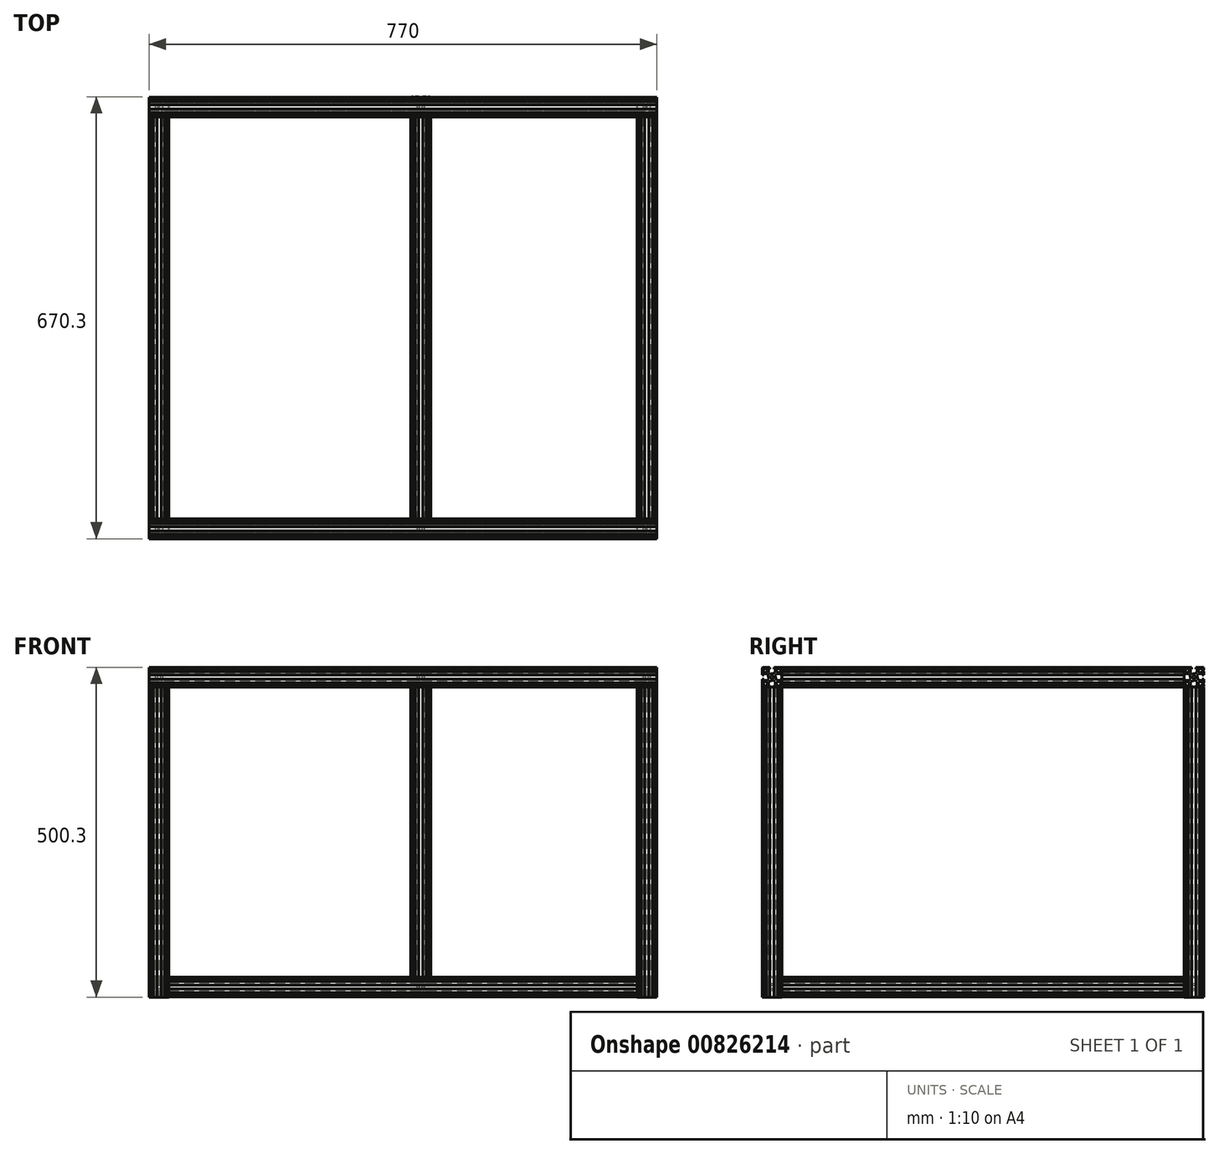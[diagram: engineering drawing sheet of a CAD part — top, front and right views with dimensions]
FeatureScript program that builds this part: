
annotation { "Feature Type Name" : "Feature", "Feature Type Description" : "" }
export const myFeature = defineFeature(function(context is Context, id is Id, definition is map)
    precondition{}
    {
        {
            var Q0;
            Q0=qCreatedBy(makeId("Top.planeOp"),FACE);
            var sketch = newSketch(context, id + "F0", { "sketchPlane" : qUnion([Q0])});
            skLineSegment(sketch, "E0", {"start": v(-2.6, 15) * mm, "end": v(32.7, 15) * mm});
            skLineSegment(sketch, "E1", {"start": v(15, 32.3) * mm, "end": v(15, -1.8) * mm});
            skLineSegment(sketch, "E2", {"start": v(19.2, 25) * mm, "end": v(32.7, 25) * mm});
            skLineSegment(sketch, "E3", {"start": v(25, 32.3) * mm, "end": v(25, 18.9) * mm});
            skLineSegment(sketch, "E4", {"start": v(10.8, 25) * mm, "end": v(-2.7, 25) * mm});
            skLineSegment(sketch, "E5", {"start": v(5, 32.3) * mm, "end": v(5, 18.9) * mm});
            skLineSegment(sketch, "E6", {"start": v(19.2, 5) * mm, "end": v(32.7, 5) * mm});
            skLineSegment(sketch, "E7", {"start": v(10.8, 5) * mm, "end": v(-2.7, 5) * mm});
            skLineSegment(sketch, "E8", {"start": v(5, -2.3) * mm, "end": v(5, 11.1) * mm});
            skLineSegment(sketch, "E9", {"start": v(18.15, 30) * mm, "end": v(18.15, 27.5) * mm});
            skLineSegment(sketch, "E10", {"start": v(20.15, 27.5) * mm, "end": v(20.15, 21.55) * mm});
            skLineSegment(sketch, "E11", {"start": v(18.15, 27.5) * mm, "end": v(20.15, 27.5) * mm});
            skLineSegment(sketch, "E12", {"start": v(11.85, 30) * mm, "end": v(11.85, 27.5) * mm});
            skLineSegment(sketch, "E13", {"start": v(11.85, 27.5) * mm, "end": v(9.85, 27.5) * mm});
            skLineSegment(sketch, "E14", {"start": v(9.85, 27.5) * mm, "end": v(9.85, 21.55) * mm});
            skLineSegment(sketch, "E15", {"start": v(0, 18.15) * mm, "end": v(2.5, 18.15) * mm});
            skLineSegment(sketch, "E16", {"start": v(2.5, 20.15) * mm, "end": v(8.45, 20.15) * mm});
            skLineSegment(sketch, "E17", {"start": v(2.5, 18.15) * mm, "end": v(2.5, 20.15) * mm});
            skLineSegment(sketch, "E18", {"start": v(0, 11.85) * mm, "end": v(2.5, 11.85) * mm});
            skLineSegment(sketch, "E19", {"start": v(2.5, 11.85) * mm, "end": v(2.5, 9.85) * mm});
            skLineSegment(sketch, "E20", {"start": v(2.5, 9.85) * mm, "end": v(8.45, 9.85) * mm});
            skLineSegment(sketch, "E21", {"start": v(11.85, 0) * mm, "end": v(11.85, 2.5) * mm});
            skLineSegment(sketch, "E22", {"start": v(9.85, 2.5) * mm, "end": v(9.85, 8.45) * mm});
            skLineSegment(sketch, "E23", {"start": v(11.85, 2.5) * mm, "end": v(9.85, 2.5) * mm});
            skLineSegment(sketch, "E24", {"start": v(18.15, 0) * mm, "end": v(18.15, 2.5) * mm});
            skLineSegment(sketch, "E25", {"start": v(18.15, 2.5) * mm, "end": v(20.15, 2.5) * mm});
            skLineSegment(sketch, "E26", {"start": v(20.15, 2.5) * mm, "end": v(20.15, 8.45) * mm});
            skLineSegment(sketch, "E27", {"start": v(30, 11.85) * mm, "end": v(27.5, 11.85) * mm});
            skLineSegment(sketch, "E28", {"start": v(27.5, 9.85) * mm, "end": v(21.55, 9.85) * mm});
            skLineSegment(sketch, "E29", {"start": v(27.5, 11.85) * mm, "end": v(27.5, 9.85) * mm});
            skLineSegment(sketch, "E30", {"start": v(30, 18.15) * mm, "end": v(27.5, 18.15) * mm});
            skLineSegment(sketch, "E31", {"start": v(27.5, 18.15) * mm, "end": v(27.5, 20.15) * mm});
            skLineSegment(sketch, "E32", {"start": v(27.5, 20.15) * mm, "end": v(21.55, 20.15) * mm});
            skLineSegment(sketch, "E33", {"start": v(11.85, 19.5) * mm, "end": v(11.85, 21.55) * mm});
            skLineSegment(sketch, "E34", {"start": v(9.85, 21.55) * mm, "end": v(11.85, 21.55) * mm});
            skLineSegment(sketch, "E35", {"start": v(11.85, 19.5) * mm, "end": v(20.15, 21.55) * mm});
            skLineSegment(sketch, "E36", {"start": v(10.5, 11.85) * mm, "end": v(8.45, 11.85) * mm});
            skLineSegment(sketch, "E37", {"start": v(8.45, 9.85) * mm, "end": v(8.45, 11.85) * mm});
            skLineSegment(sketch, "E38", {"start": v(10.5, 11.85) * mm, "end": v(8.45, 20.15) * mm});
            skLineSegment(sketch, "E39", {"start": v(18.15, 10.5) * mm, "end": v(18.15, 8.45) * mm});
            skLineSegment(sketch, "E40", {"start": v(20.15, 8.45) * mm, "end": v(18.15, 8.45) * mm});
            skLineSegment(sketch, "E41", {"start": v(18.15, 10.5) * mm, "end": v(9.85, 8.45) * mm});
            skLineSegment(sketch, "E42", {"start": v(19.5, 18.15) * mm, "end": v(21.55, 18.15) * mm});
            skLineSegment(sketch, "E43", {"start": v(21.55, 20.15) * mm, "end": v(21.55, 18.15) * mm});
            skLineSegment(sketch, "E44", {"start": v(19.5, 18.15) * mm, "end": v(21.55, 9.85) * mm});
            skCircle(sketch, "E45", {"center": v(15, 15) * mm, "radius": 2.5 * mm});
            skLineSegment(sketch, "E46", {"start": v(28, 26.24) * mm, "end": v(26.24, 28) * mm});
            skLineSegment(sketch, "E47", {"start": v(26.24, 28) * mm, "end": v(23.76, 28) * mm});
            skLineSegment(sketch, "E48", {"start": v(23.76, 28) * mm, "end": v(22, 26.24) * mm});
            skLineSegment(sketch, "E49", {"start": v(22, 26.24) * mm, "end": v(22, 23.76) * mm});
            skLineSegment(sketch, "E50", {"start": v(22, 23.76) * mm, "end": v(23.76, 22) * mm});
            skLineSegment(sketch, "E51", {"start": v(23.76, 22) * mm, "end": v(26.24, 22) * mm});
            skLineSegment(sketch, "E52", {"start": v(26.24, 22) * mm, "end": v(28, 23.76) * mm});
            skLineSegment(sketch, "E53", {"start": v(28, 23.76) * mm, "end": v(28, 26.24) * mm});
            skLineSegment(sketch, "E54", {"start": v(8, 26.24) * mm, "end": v(6.24, 28) * mm});
            skLineSegment(sketch, "E55", {"start": v(6.24, 28) * mm, "end": v(3.76, 28) * mm});
            skLineSegment(sketch, "E56", {"start": v(3.76, 28) * mm, "end": v(2, 26.24) * mm});
            skLineSegment(sketch, "E57", {"start": v(2, 26.24) * mm, "end": v(2, 23.76) * mm});
            skLineSegment(sketch, "E58", {"start": v(2, 23.76) * mm, "end": v(3.76, 22) * mm});
            skLineSegment(sketch, "E59", {"start": v(3.76, 22) * mm, "end": v(6.24, 22) * mm});
            skLineSegment(sketch, "E60", {"start": v(6.24, 22) * mm, "end": v(8, 23.76) * mm});
            skLineSegment(sketch, "E61", {"start": v(8, 23.76) * mm, "end": v(8, 26.24) * mm});
            skLineSegment(sketch, "E62", {"start": v(28, 6.24) * mm, "end": v(26.24, 8) * mm});
            skLineSegment(sketch, "E63", {"start": v(26.24, 8) * mm, "end": v(23.76, 8) * mm});
            skLineSegment(sketch, "E64", {"start": v(23.76, 8) * mm, "end": v(22, 6.24) * mm});
            skLineSegment(sketch, "E65", {"start": v(22, 6.24) * mm, "end": v(22, 3.76) * mm});
            skLineSegment(sketch, "E66", {"start": v(22, 3.76) * mm, "end": v(23.76, 2) * mm});
            skLineSegment(sketch, "E67", {"start": v(23.76, 2) * mm, "end": v(26.24, 2) * mm});
            skLineSegment(sketch, "E68", {"start": v(26.24, 2) * mm, "end": v(28, 3.76) * mm});
            skLineSegment(sketch, "E69", {"start": v(28, 3.76) * mm, "end": v(28, 6.24) * mm});
            skLineSegment(sketch, "E70", {"start": v(8, 6.24) * mm, "end": v(6.24, 8) * mm});
            skLineSegment(sketch, "E71", {"start": v(6.24, 8) * mm, "end": v(3.76, 8) * mm});
            skLineSegment(sketch, "E72", {"start": v(3.76, 8) * mm, "end": v(2, 6.24) * mm});
            skLineSegment(sketch, "E73", {"start": v(2, 6.24) * mm, "end": v(2, 3.76) * mm});
            skLineSegment(sketch, "E74", {"start": v(2, 3.76) * mm, "end": v(3.76, 2) * mm});
            skLineSegment(sketch, "E75", {"start": v(3.76, 2) * mm, "end": v(6.24, 2) * mm});
            skLineSegment(sketch, "E76", {"start": v(6.24, 2) * mm, "end": v(8, 3.76) * mm});
            skLineSegment(sketch, "E77", {"start": v(8, 3.76) * mm, "end": v(8, 6.24) * mm});
            skLineSegment(sketch, "E78", {"start": v(26.5, 30) * mm, "end": v(26.5, 29.7) * mm});
            skLineSegment(sketch, "E79", {"start": v(26.5, 29.7) * mm, "end": v(25, 29.7) * mm});
            skLineSegment(sketch, "E80", {"start": v(23.5, 30) * mm, "end": v(23.5, 29.7) * mm});
            skLineSegment(sketch, "E81", {"start": v(23.5, 29.7) * mm, "end": v(25, 29.7) * mm});
            skLineSegment(sketch, "E82", {"start": v(30, 23.5) * mm, "end": v(29.7, 23.5) * mm});
            skLineSegment(sketch, "E83", {"start": v(29.7, 23.5) * mm, "end": v(29.7, 25) * mm});
            skLineSegment(sketch, "E84", {"start": v(30, 26.5) * mm, "end": v(29.7, 26.5) * mm});
            skLineSegment(sketch, "E85", {"start": v(29.7, 26.5) * mm, "end": v(29.7, 25) * mm});
            skLineSegment(sketch, "E86", {"start": v(25, -2.3) * mm, "end": v(25, 11.1) * mm});
            skLineSegment(sketch, "E87", {"start": v(26.5, 0) * mm, "end": v(26.5, 0.3) * mm});
            skLineSegment(sketch, "E88", {"start": v(26.5, 0.3) * mm, "end": v(25, 0.3) * mm});
            skLineSegment(sketch, "E89", {"start": v(23.5, 0) * mm, "end": v(23.5, 0.3) * mm});
            skLineSegment(sketch, "E90", {"start": v(23.5, 0.3) * mm, "end": v(25, 0.3) * mm});
            skLineSegment(sketch, "E91", {"start": v(30, 6.5) * mm, "end": v(29.7, 6.5) * mm});
            skLineSegment(sketch, "E92", {"start": v(29.7, 6.5) * mm, "end": v(29.7, 5) * mm});
            skLineSegment(sketch, "E93", {"start": v(30, 3.5) * mm, "end": v(29.7, 3.5) * mm});
            skLineSegment(sketch, "E94", {"start": v(29.7, 3.5) * mm, "end": v(29.7, 5) * mm});
            skLineSegment(sketch, "E95", {"start": v(3.5, 30) * mm, "end": v(3.5, 29.7) * mm});
            skLineSegment(sketch, "E96", {"start": v(3.5, 29.7) * mm, "end": v(5, 29.7) * mm});
            skLineSegment(sketch, "E97", {"start": v(6.5, 30) * mm, "end": v(6.5, 29.7) * mm});
            skLineSegment(sketch, "E98", {"start": v(6.5, 29.7) * mm, "end": v(5, 29.7) * mm});
            skLineSegment(sketch, "E99", {"start": v(0, 23.5) * mm, "end": v(0.3, 23.5) * mm});
            skLineSegment(sketch, "E100", {"start": v(0.3, 23.5) * mm, "end": v(0.3, 25) * mm});
            skLineSegment(sketch, "E101", {"start": v(0, 26.5) * mm, "end": v(0.3, 26.5) * mm});
            skLineSegment(sketch, "E102", {"start": v(0.3, 26.5) * mm, "end": v(0.3, 25) * mm});
            skLineSegment(sketch, "E103", {"start": v(0, 6.5) * mm, "end": v(0.3, 6.5) * mm});
            skLineSegment(sketch, "E104", {"start": v(0.3, 6.5) * mm, "end": v(0.3, 5) * mm});
            skLineSegment(sketch, "E105", {"start": v(0, 3.5) * mm, "end": v(0.3, 3.5) * mm});
            skLineSegment(sketch, "E106", {"start": v(0.3, 3.5) * mm, "end": v(0.3, 5) * mm});
            skLineSegment(sketch, "E107", {"start": v(3.5, 0) * mm, "end": v(3.5, 0.3) * mm});
            skLineSegment(sketch, "E108", {"start": v(3.5, 0.3) * mm, "end": v(5, 0.3) * mm});
            skLineSegment(sketch, "E109", {"start": v(6.5, 0) * mm, "end": v(6.5, 0.3) * mm});
            skLineSegment(sketch, "E110", {"start": v(6.5, 0.3) * mm, "end": v(5, 0.3) * mm});
            skLineSegment(sketch, "E111", {"start": v(29, 30) * mm, "end": v(26.5, 30) * mm});
            skLineSegment(sketch, "E112", {"start": v(23.5, 30) * mm, "end": v(18.15, 30) * mm});
            skLineSegment(sketch, "E113", {"start": v(30, 18.15) * mm, "end": v(30, 23.5) * mm});
            skLineSegment(sketch, "E114", {"start": v(30, 29) * mm, "end": v(30, 26.5) * mm});
            skLineSegment(sketch, "E115", {"start": v(30, 1) * mm, "end": v(30, 3.5) * mm});
            skLineSegment(sketch, "E116", {"start": v(30, 6.5) * mm, "end": v(30, 11.85) * mm});
            skLineSegment(sketch, "E117", {"start": v(18.15, 0) * mm, "end": v(23.5, 0) * mm});
            skLineSegment(sketch, "E118", {"start": v(29, 0) * mm, "end": v(26.5, 0) * mm});
            skLineSegment(sketch, "E119", {"start": v(1, 0) * mm, "end": v(3.5, 0) * mm});
            skLineSegment(sketch, "E120", {"start": v(6.5, 0) * mm, "end": v(11.85, 0) * mm});
            skLineSegment(sketch, "E121", {"start": v(0, 11.85) * mm, "end": v(0, 6.5) * mm});
            skLineSegment(sketch, "E122", {"start": v(0, 1) * mm, "end": v(0, 3.5) * mm});
            skLineSegment(sketch, "E123", {"start": v(0, 29) * mm, "end": v(0, 26.5) * mm});
            skLineSegment(sketch, "E124", {"start": v(0, 23.5) * mm, "end": v(0, 18.15) * mm});
            skLineSegment(sketch, "E125", {"start": v(11.85, 30) * mm, "end": v(6.5, 30) * mm});
            skLineSegment(sketch, "E126", {"start": v(1, 30) * mm, "end": v(3.5, 30) * mm});
            skLineSegment(sketch, "E127", {"start": v(1, 30) * mm, "end": v(0, 29) * mm});
            skLineSegment(sketch, "E128", {"start": v(0, 1) * mm, "end": v(1, 0) * mm});
            skLineSegment(sketch, "E129", {"start": v(29, 0) * mm, "end": v(30, 1) * mm});
            skLineSegment(sketch, "E130", {"start": v(30, 29) * mm, "end": v(29, 30) * mm});
            skSolve(sketch);
        }
        {
            var Q0;
            {var subQ0=sQuery(id+"F0.wireOp",EDGE,"E76");Q0=makeQuery(id+"F0.imprint","IMPRINT",FACE,{"disambiguationData":[TD([[makeQuery(id+"F0.imprint","IMPRINT",EDGE,{"derivedFrom":subQ0}),1.0]])]});}
            var Q1;
            {var subQ0=sQuery(id+"F0.wireOp",EDGE,"E72");Q1=makeQuery(id+"F0.imprint","IMPRINT",FACE,{"disambiguationData":[TD([[makeQuery(id+"F0.imprint","IMPRINT",EDGE,{"derivedFrom":subQ0}),1.0]])]});}
            var Q2;
            {var subQ1=sQuery(id+"F0.wireOp",EDGE,"E70");Q2=makeQuery(id+"F0.imprint","IMPRINT",FACE,{"disambiguationData":[TD([[makeQuery(id+"F0.imprint","IMPRINT",EDGE,{"derivedFrom":subQ1}),1.0]])]});}
            var Q3;
            {var subQ6=sQuery(id+"F0.wireOp",EDGE,"E74");Q3=makeQuery(id+"F0.imprint","IMPRINT",FACE,{"disambiguationData":[TD([[makeQuery(id+"F0.imprint","IMPRINT",EDGE,{"derivedFrom":subQ6}),-1.0]])]});}
            var Q4;
            {var subQ0=sQuery(id+"F0.wireOp",EDGE,"E74");Q4=makeQuery(id+"F0.imprint","IMPRINT",FACE,{"disambiguationData":[TD([[makeQuery(id+"F0.imprint","IMPRINT",EDGE,{"derivedFrom":subQ0}),1.0]])]});}
            var Q5;
            {var subQ12=sQuery(id+"F0.wireOp",EDGE,"E33");Q5=makeQuery(id+"F0.imprint","IMPRINT",FACE,{"disambiguationData":[TD([[makeQuery(id+"F0.imprint","IMPRINT",EDGE,{"derivedFrom":subQ12}),1.0]])]});}
            var Q6;
            {var subQ1=sQuery(id+"F0.wireOp",EDGE,"E56");Q6=makeQuery(id+"F0.imprint","IMPRINT",FACE,{"disambiguationData":[TD([[makeQuery(id+"F0.imprint","IMPRINT",EDGE,{"derivedFrom":subQ1}),-1.0]])]});}
            var Q7;
            Q7=makeQuery(id+"F0.imprint","IMPRINT",FACE,{"disambiguationData":[TD([[makeQuery(id+"F0.imprint","IMPRINT",EDGE,{"derivedFrom":sQuery(id+"F0.wireOp",EDGE,"E15")}),1.0]])]});
            var Q8;
            {var subQ1=sQuery(id+"F0.wireOp",EDGE,"E36");Q8=makeQuery(id+"F0.imprint","IMPRINT",FACE,{"disambiguationData":[TD([[makeQuery(id+"F0.imprint","IMPRINT",EDGE,{"derivedFrom":subQ1}),1.0]])]});}
            var Q9;
            Q9=makeQuery(id+"F0.imprint","IMPRINT",FACE,{"disambiguationData":[TD([[makeQuery(id+"F0.imprint","IMPRINT",EDGE,{"derivedFrom":sQuery(id+"F0.wireOp",EDGE,"E24")}),-1.0]])]});
            var Q10;
            {var subQ5=sQuery(id+"F0.wireOp",EDGE,"E42");Q10=makeQuery(id+"F0.imprint","IMPRINT",FACE,{"disambiguationData":[TD([[makeQuery(id+"F0.imprint","IMPRINT",EDGE,{"derivedFrom":subQ5}),1.0]])]});}
            var Q11;
            {var subQ1=sQuery(id+"F0.wireOp",EDGE,"E64");Q11=makeQuery(id+"F0.imprint","IMPRINT",FACE,{"disambiguationData":[TD([[makeQuery(id+"F0.imprint","IMPRINT",EDGE,{"derivedFrom":subQ1}),1.0]])]});}
            var Q12;
            {var subQ6=sQuery(id+"F0.wireOp",EDGE,"E39");Q12=makeQuery(id+"F0.imprint","IMPRINT",FACE,{"disambiguationData":[TD([[makeQuery(id+"F0.imprint","IMPRINT",EDGE,{"derivedFrom":subQ6}),1.0]])]});}
            var Q13;
            {var subQ1=sQuery(id+"F0.wireOp",EDGE,"E66");Q13=makeQuery(id+"F0.imprint","IMPRINT",FACE,{"disambiguationData":[TD([[makeQuery(id+"F0.imprint","IMPRINT",EDGE,{"derivedFrom":subQ1}),1.0]])]});}
            var Q14;
            {var subQ1=sQuery(id+"F0.wireOp",EDGE,"E62");Q14=makeQuery(id+"F0.imprint","IMPRINT",FACE,{"disambiguationData":[TD([[makeQuery(id+"F0.imprint","IMPRINT",EDGE,{"derivedFrom":subQ1}),1.0]])]});}
            var Q15;
            {var subQ1=sQuery(id+"F0.wireOp",EDGE,"E68");Q15=makeQuery(id+"F0.imprint","IMPRINT",FACE,{"disambiguationData":[TD([[makeQuery(id+"F0.imprint","IMPRINT",EDGE,{"derivedFrom":subQ1}),1.0]])]});}
            var Q16;
            {var subQ0=sQuery(id+"F0.wireOp",EDGE,"E58");Q16=makeQuery(id+"F0.imprint","IMPRINT",FACE,{"disambiguationData":[TD([[makeQuery(id+"F0.imprint","IMPRINT",EDGE,{"derivedFrom":subQ0}),1.0]])]});}
            var Q17;
            {var subQ0=sQuery(id+"F0.wireOp",EDGE,"E60");Q17=makeQuery(id+"F0.imprint","IMPRINT",FACE,{"disambiguationData":[TD([[makeQuery(id+"F0.imprint","IMPRINT",EDGE,{"derivedFrom":subQ0}),1.0]])]});}
            var Q18;
            {var subQ0=sQuery(id+"F0.wireOp",EDGE,"E56");Q18=makeQuery(id+"F0.imprint","IMPRINT",FACE,{"disambiguationData":[TD([[makeQuery(id+"F0.imprint","IMPRINT",EDGE,{"derivedFrom":subQ0}),1.0]])]});}
            var Q19;
            {var subQ0=sQuery(id+"F0.wireOp",EDGE,"E45");var subQ1=sQuery(id+"F0.wireOp",EDGE,"E0");var subQ2=makeQuery(id+"F0.imprint","INTERSECT",VERTEX,{"disambiguationData":[OD(0.0)],"derivedFrom":[subQ1,subQ0]});Q19=makeQuery(id+"F0.imprint","IMPRINT",FACE,{"disambiguationData":[TD([[makeQuery(id+"F0.imprint","IMPRINT",EDGE,{"disambiguationData":[TD([[subQ2,-1.0]])],"derivedFrom":subQ1}),1.0]])]});}
            var Q20;
            {var subQ0=sQuery(id+"F0.wireOp",EDGE,"E45");var subQ1=sQuery(id+"F0.wireOp",EDGE,"E0");var subQ2=makeQuery(id+"F0.imprint","INTERSECT",VERTEX,{"disambiguationData":[OD(0.0)],"derivedFrom":[subQ1,subQ0]});Q20=makeQuery(id+"F0.imprint","IMPRINT",FACE,{"disambiguationData":[TD([[makeQuery(id+"F0.imprint","IMPRINT",EDGE,{"disambiguationData":[TD([[subQ2,-1.0]])],"derivedFrom":subQ1}),-1.0]])]});}
            var Q21;
            {var subQ0=sQuery(id+"F0.wireOp",EDGE,"E1");var subQ1=sQuery(id+"F0.wireOp",EDGE,"E0");var subQ2=makeQuery(id+"F0.imprint","INTERSECT",VERTEX,{"derivedFrom":[subQ1,subQ0]});Q21=makeQuery(id+"F0.imprint","IMPRINT",FACE,{"disambiguationData":[TD([[makeQuery(id+"F0.imprint","IMPRINT",EDGE,{"disambiguationData":[TD([[subQ2,-1.0]])],"derivedFrom":subQ1}),1.0]])]});}
            var Q22;
            {var subQ0=sQuery(id+"F0.wireOp",EDGE,"E1");var subQ1=sQuery(id+"F0.wireOp",EDGE,"E0");var subQ2=makeQuery(id+"F0.imprint","INTERSECT",VERTEX,{"derivedFrom":[subQ1,subQ0]});Q22=makeQuery(id+"F0.imprint","IMPRINT",FACE,{"disambiguationData":[TD([[makeQuery(id+"F0.imprint","IMPRINT",EDGE,{"disambiguationData":[TD([[subQ2,-1.0]])],"derivedFrom":subQ1}),-1.0]])]});}
            var Q23;
            Q23=makeQuery(id+"F0.imprint","IMPRINT",FACE,{"disambiguationData":[TD([[makeQuery(id+"F0.imprint","IMPRINT",EDGE,{"derivedFrom":sQuery(id+"F0.wireOp",EDGE,"E9")}),1.0]])]});
            var Q24;
            {var subQ0=sQuery(id+"F0.wireOp",EDGE,"E48");Q24=makeQuery(id+"F0.imprint","IMPRINT",FACE,{"disambiguationData":[TD([[makeQuery(id+"F0.imprint","IMPRINT",EDGE,{"derivedFrom":subQ0}),1.0]])]});}
            var Q25;
            {var subQ0=sQuery(id+"F0.wireOp",EDGE,"E50");Q25=makeQuery(id+"F0.imprint","IMPRINT",FACE,{"disambiguationData":[TD([[makeQuery(id+"F0.imprint","IMPRINT",EDGE,{"derivedFrom":subQ0}),1.0]])]});}
            var Q26;
            {var subQ1=sQuery(id+"F0.wireOp",EDGE,"E46");Q26=makeQuery(id+"F0.imprint","IMPRINT",FACE,{"disambiguationData":[TD([[makeQuery(id+"F0.imprint","IMPRINT",EDGE,{"derivedFrom":subQ1}),1.0]])]});}
            var Q27;
            {var subQ0=sQuery(id+"F0.wireOp",EDGE,"E52");Q27=makeQuery(id+"F0.imprint","IMPRINT",FACE,{"disambiguationData":[TD([[makeQuery(id+"F0.imprint","IMPRINT",EDGE,{"derivedFrom":subQ0}),1.0]])]});}
            var Q28;
            {var subQ5=sQuery(id+"F0.wireOp",EDGE,"E46");Q28=makeQuery(id+"F0.imprint","IMPRINT",FACE,{"disambiguationData":[TD([[makeQuery(id+"F0.imprint","IMPRINT",EDGE,{"derivedFrom":subQ5}),-1.0]])]});}
            var Q29;
            Q29=makeQuery(id+"F0.imprint","IMPRINT",FACE,{"disambiguationData":[TD([[makeQuery(id+"F0.imprint","IMPRINT",EDGE,{"derivedFrom":sQuery(id+"F0.wireOp",EDGE,"E30")}),-1.0]])]});
            var Q30;
            Q30=makeQuery(id+"F0.imprint","IMPRINT",FACE,{"disambiguationData":[TD([[makeQuery(id+"F0.imprint","IMPRINT",EDGE,{"derivedFrom":sQuery(id+"F0.wireOp",EDGE,"E12")}),-1.0]])]});
            var Q31;
            {var subQ0=sQuery(id+"F0.wireOp",EDGE,"E54");Q31=makeQuery(id+"F0.imprint","IMPRINT",FACE,{"disambiguationData":[TD([[makeQuery(id+"F0.imprint","IMPRINT",EDGE,{"derivedFrom":subQ0}),1.0]])]});}
            var Q32;
            Q32=makeQuery(id+"F0.imprint","IMPRINT",FACE,{"disambiguationData":[TD([[makeQuery(id+"F0.imprint","IMPRINT",EDGE,{"derivedFrom":sQuery(id+"F0.wireOp",EDGE,"E27")}),1.0]])]});
            var Q33;
            {var subQ8=sQuery(id+"F0.wireOp",EDGE,"E68");Q33=makeQuery(id+"F0.imprint","IMPRINT",FACE,{"disambiguationData":[TD([[makeQuery(id+"F0.imprint","IMPRINT",EDGE,{"derivedFrom":subQ8}),-1.0]])]});}
            var Q34;
            Q34=makeQuery(id+"F0.imprint","IMPRINT",FACE,{"disambiguationData":[TD([[makeQuery(id+"F0.imprint","IMPRINT",EDGE,{"derivedFrom":sQuery(id+"F0.wireOp",EDGE,"E18")}),-1.0]])]});
            var Q35;
            Q35=makeQuery(id+"F0.imprint","IMPRINT",FACE,{"disambiguationData":[TD([[makeQuery(id+"F0.imprint","IMPRINT",EDGE,{"derivedFrom":sQuery(id+"F0.wireOp",EDGE,"E21")}),1.0]])]});
            extrude(context, id + "F1", {"entities" : qUnion([Q0, Q1, Q2, Q3, Q4, Q5, Q6, Q7, Q8, Q9, Q10, Q11, Q12, Q13, Q14, Q15, Q16, Q17, Q18, Q19, Q20, Q21, Q22, Q23, Q24, Q25, Q26, Q27, Q28, Q29, Q30, Q31, Q32, Q33, Q34, Q35]), "depth" : 470 * mm, "offsetDistance" : 25 * mm});
        }
        {
            var Q0;
            Q0=makeQuery(id+"F1.opExtrude","SWEPT_BODY",BODY,{"disambiguationData":[OSD([sQuery(id+"F0.wireOp",EDGE,"E9"),sQuery(id+"F0.wireOp",EDGE,"E10"),sQuery(id+"F0.wireOp",EDGE,"E11"),sQuery(id+"F0.wireOp",EDGE,"E12"),sQuery(id+"F0.wireOp",EDGE,"E13"),sQuery(id+"F0.wireOp",EDGE,"E14"),sQuery(id+"F0.wireOp",EDGE,"E15"),sQuery(id+"F0.wireOp",EDGE,"E16"),sQuery(id+"F0.wireOp",EDGE,"E17"),sQuery(id+"F0.wireOp",EDGE,"E18"),sQuery(id+"F0.wireOp",EDGE,"E19"),sQuery(id+"F0.wireOp",EDGE,"E20"),sQuery(id+"F0.wireOp",EDGE,"E21"),sQuery(id+"F0.wireOp",EDGE,"E22"),sQuery(id+"F0.wireOp",EDGE,"E23"),sQuery(id+"F0.wireOp",EDGE,"E24"),sQuery(id+"F0.wireOp",EDGE,"E25"),sQuery(id+"F0.wireOp",EDGE,"E26"),sQuery(id+"F0.wireOp",EDGE,"E27"),sQuery(id+"F0.wireOp",EDGE,"E28"),sQuery(id+"F0.wireOp",EDGE,"E29"),sQuery(id+"F0.wireOp",EDGE,"E30"),sQuery(id+"F0.wireOp",EDGE,"E31"),sQuery(id+"F0.wireOp",EDGE,"E32"),sQuery(id+"F0.wireOp",EDGE,"E33"),sQuery(id+"F0.wireOp",EDGE,"E34"),sQuery(id+"F0.wireOp",EDGE,"E35"),sQuery(id+"F0.wireOp",EDGE,"E36"),sQuery(id+"F0.wireOp",EDGE,"E37"),sQuery(id+"F0.wireOp",EDGE,"E38"),sQuery(id+"F0.wireOp",EDGE,"E39"),sQuery(id+"F0.wireOp",EDGE,"E40"),sQuery(id+"F0.wireOp",EDGE,"E41"),sQuery(id+"F0.wireOp",EDGE,"E42"),sQuery(id+"F0.wireOp",EDGE,"E43"),sQuery(id+"F0.wireOp",EDGE,"E44"),sQuery(id+"F0.wireOp",EDGE,"E78"),sQuery(id+"F0.wireOp",EDGE,"E79"),sQuery(id+"F0.wireOp",EDGE,"E80"),sQuery(id+"F0.wireOp",EDGE,"E81"),sQuery(id+"F0.wireOp",EDGE,"E82"),sQuery(id+"F0.wireOp",EDGE,"E83"),sQuery(id+"F0.wireOp",EDGE,"E84"),sQuery(id+"F0.wireOp",EDGE,"E85"),sQuery(id+"F0.wireOp",EDGE,"E87"),sQuery(id+"F0.wireOp",EDGE,"E88"),sQuery(id+"F0.wireOp",EDGE,"E89"),sQuery(id+"F0.wireOp",EDGE,"E90"),sQuery(id+"F0.wireOp",EDGE,"E91"),sQuery(id+"F0.wireOp",EDGE,"E92"),sQuery(id+"F0.wireOp",EDGE,"E93"),sQuery(id+"F0.wireOp",EDGE,"E94"),sQuery(id+"F0.wireOp",EDGE,"E95"),sQuery(id+"F0.wireOp",EDGE,"E96"),sQuery(id+"F0.wireOp",EDGE,"E97"),sQuery(id+"F0.wireOp",EDGE,"E98"),sQuery(id+"F0.wireOp",EDGE,"E99"),sQuery(id+"F0.wireOp",EDGE,"E100"),sQuery(id+"F0.wireOp",EDGE,"E101"),sQuery(id+"F0.wireOp",EDGE,"E102"),sQuery(id+"F0.wireOp",EDGE,"E103"),sQuery(id+"F0.wireOp",EDGE,"E104"),sQuery(id+"F0.wireOp",EDGE,"E105"),sQuery(id+"F0.wireOp",EDGE,"E106"),sQuery(id+"F0.wireOp",EDGE,"E107"),sQuery(id+"F0.wireOp",EDGE,"E108"),sQuery(id+"F0.wireOp",EDGE,"E109"),sQuery(id+"F0.wireOp",EDGE,"E110"),sQuery(id+"F0.wireOp",EDGE,"E111"),sQuery(id+"F0.wireOp",EDGE,"E112"),sQuery(id+"F0.wireOp",EDGE,"E113"),sQuery(id+"F0.wireOp",EDGE,"E114"),sQuery(id+"F0.wireOp",EDGE,"E115"),sQuery(id+"F0.wireOp",EDGE,"E116"),sQuery(id+"F0.wireOp",EDGE,"E117"),sQuery(id+"F0.wireOp",EDGE,"E118"),sQuery(id+"F0.wireOp",EDGE,"E119"),sQuery(id+"F0.wireOp",EDGE,"E120"),sQuery(id+"F0.wireOp",EDGE,"E121"),sQuery(id+"F0.wireOp",EDGE,"E122"),sQuery(id+"F0.wireOp",EDGE,"E123"),sQuery(id+"F0.wireOp",EDGE,"E124"),sQuery(id+"F0.wireOp",EDGE,"E125"),sQuery(id+"F0.wireOp",EDGE,"E126"),sQuery(id+"F0.wireOp",EDGE,"E127"),sQuery(id+"F0.wireOp",EDGE,"E128"),sQuery(id+"F0.wireOp",EDGE,"E129"),sQuery(id+"F0.wireOp",EDGE,"E130")])]});
            transform(context, id + "F2", {"entities" : qUnion([Q0]), "transformType" : TransformType.TRANSLATION_3D, "dx" : 0 * mm, "dy" : 640 * mm, "dz" : 0 * mm, "makeCopy" : true});
        }
        {
            var Q0;
            Q0=makeQuery(id+"F1.opExtrude","SWEPT_BODY",BODY,{"disambiguationData":[OSD([sQuery(id+"F0.wireOp",EDGE,"E9"),sQuery(id+"F0.wireOp",EDGE,"E10"),sQuery(id+"F0.wireOp",EDGE,"E11"),sQuery(id+"F0.wireOp",EDGE,"E12"),sQuery(id+"F0.wireOp",EDGE,"E13"),sQuery(id+"F0.wireOp",EDGE,"E14"),sQuery(id+"F0.wireOp",EDGE,"E15"),sQuery(id+"F0.wireOp",EDGE,"E16"),sQuery(id+"F0.wireOp",EDGE,"E17"),sQuery(id+"F0.wireOp",EDGE,"E18"),sQuery(id+"F0.wireOp",EDGE,"E19"),sQuery(id+"F0.wireOp",EDGE,"E20"),sQuery(id+"F0.wireOp",EDGE,"E21"),sQuery(id+"F0.wireOp",EDGE,"E22"),sQuery(id+"F0.wireOp",EDGE,"E23"),sQuery(id+"F0.wireOp",EDGE,"E24"),sQuery(id+"F0.wireOp",EDGE,"E25"),sQuery(id+"F0.wireOp",EDGE,"E26"),sQuery(id+"F0.wireOp",EDGE,"E27"),sQuery(id+"F0.wireOp",EDGE,"E28"),sQuery(id+"F0.wireOp",EDGE,"E29"),sQuery(id+"F0.wireOp",EDGE,"E30"),sQuery(id+"F0.wireOp",EDGE,"E31"),sQuery(id+"F0.wireOp",EDGE,"E32"),sQuery(id+"F0.wireOp",EDGE,"E33"),sQuery(id+"F0.wireOp",EDGE,"E34"),sQuery(id+"F0.wireOp",EDGE,"E35"),sQuery(id+"F0.wireOp",EDGE,"E36"),sQuery(id+"F0.wireOp",EDGE,"E37"),sQuery(id+"F0.wireOp",EDGE,"E38"),sQuery(id+"F0.wireOp",EDGE,"E39"),sQuery(id+"F0.wireOp",EDGE,"E40"),sQuery(id+"F0.wireOp",EDGE,"E41"),sQuery(id+"F0.wireOp",EDGE,"E42"),sQuery(id+"F0.wireOp",EDGE,"E43"),sQuery(id+"F0.wireOp",EDGE,"E44"),sQuery(id+"F0.wireOp",EDGE,"E78"),sQuery(id+"F0.wireOp",EDGE,"E79"),sQuery(id+"F0.wireOp",EDGE,"E80"),sQuery(id+"F0.wireOp",EDGE,"E81"),sQuery(id+"F0.wireOp",EDGE,"E82"),sQuery(id+"F0.wireOp",EDGE,"E83"),sQuery(id+"F0.wireOp",EDGE,"E84"),sQuery(id+"F0.wireOp",EDGE,"E85"),sQuery(id+"F0.wireOp",EDGE,"E87"),sQuery(id+"F0.wireOp",EDGE,"E88"),sQuery(id+"F0.wireOp",EDGE,"E89"),sQuery(id+"F0.wireOp",EDGE,"E90"),sQuery(id+"F0.wireOp",EDGE,"E91"),sQuery(id+"F0.wireOp",EDGE,"E92"),sQuery(id+"F0.wireOp",EDGE,"E93"),sQuery(id+"F0.wireOp",EDGE,"E94"),sQuery(id+"F0.wireOp",EDGE,"E95"),sQuery(id+"F0.wireOp",EDGE,"E96"),sQuery(id+"F0.wireOp",EDGE,"E97"),sQuery(id+"F0.wireOp",EDGE,"E98"),sQuery(id+"F0.wireOp",EDGE,"E99"),sQuery(id+"F0.wireOp",EDGE,"E100"),sQuery(id+"F0.wireOp",EDGE,"E101"),sQuery(id+"F0.wireOp",EDGE,"E102"),sQuery(id+"F0.wireOp",EDGE,"E103"),sQuery(id+"F0.wireOp",EDGE,"E104"),sQuery(id+"F0.wireOp",EDGE,"E105"),sQuery(id+"F0.wireOp",EDGE,"E106"),sQuery(id+"F0.wireOp",EDGE,"E107"),sQuery(id+"F0.wireOp",EDGE,"E108"),sQuery(id+"F0.wireOp",EDGE,"E109"),sQuery(id+"F0.wireOp",EDGE,"E110"),sQuery(id+"F0.wireOp",EDGE,"E111"),sQuery(id+"F0.wireOp",EDGE,"E112"),sQuery(id+"F0.wireOp",EDGE,"E113"),sQuery(id+"F0.wireOp",EDGE,"E114"),sQuery(id+"F0.wireOp",EDGE,"E115"),sQuery(id+"F0.wireOp",EDGE,"E116"),sQuery(id+"F0.wireOp",EDGE,"E117"),sQuery(id+"F0.wireOp",EDGE,"E118"),sQuery(id+"F0.wireOp",EDGE,"E119"),sQuery(id+"F0.wireOp",EDGE,"E120"),sQuery(id+"F0.wireOp",EDGE,"E121"),sQuery(id+"F0.wireOp",EDGE,"E122"),sQuery(id+"F0.wireOp",EDGE,"E123"),sQuery(id+"F0.wireOp",EDGE,"E124"),sQuery(id+"F0.wireOp",EDGE,"E125"),sQuery(id+"F0.wireOp",EDGE,"E126"),sQuery(id+"F0.wireOp",EDGE,"E127"),sQuery(id+"F0.wireOp",EDGE,"E128"),sQuery(id+"F0.wireOp",EDGE,"E129"),sQuery(id+"F0.wireOp",EDGE,"E130")])]});
            var Q1;
            Q1=makeQuery(id+"F2.opPattern","COPY",BODY,{"derivedFrom":makeQuery(id+"F1.opExtrude","SWEPT_BODY",BODY,{"disambiguationData":[OSD([sQuery(id+"F0.wireOp",EDGE,"E9"),sQuery(id+"F0.wireOp",EDGE,"E10"),sQuery(id+"F0.wireOp",EDGE,"E11"),sQuery(id+"F0.wireOp",EDGE,"E12"),sQuery(id+"F0.wireOp",EDGE,"E13"),sQuery(id+"F0.wireOp",EDGE,"E14"),sQuery(id+"F0.wireOp",EDGE,"E15"),sQuery(id+"F0.wireOp",EDGE,"E16"),sQuery(id+"F0.wireOp",EDGE,"E17"),sQuery(id+"F0.wireOp",EDGE,"E18"),sQuery(id+"F0.wireOp",EDGE,"E19"),sQuery(id+"F0.wireOp",EDGE,"E20"),sQuery(id+"F0.wireOp",EDGE,"E21"),sQuery(id+"F0.wireOp",EDGE,"E22"),sQuery(id+"F0.wireOp",EDGE,"E23"),sQuery(id+"F0.wireOp",EDGE,"E24"),sQuery(id+"F0.wireOp",EDGE,"E25"),sQuery(id+"F0.wireOp",EDGE,"E26"),sQuery(id+"F0.wireOp",EDGE,"E27"),sQuery(id+"F0.wireOp",EDGE,"E28"),sQuery(id+"F0.wireOp",EDGE,"E29"),sQuery(id+"F0.wireOp",EDGE,"E30"),sQuery(id+"F0.wireOp",EDGE,"E31"),sQuery(id+"F0.wireOp",EDGE,"E32"),sQuery(id+"F0.wireOp",EDGE,"E33"),sQuery(id+"F0.wireOp",EDGE,"E34"),sQuery(id+"F0.wireOp",EDGE,"E35"),sQuery(id+"F0.wireOp",EDGE,"E36"),sQuery(id+"F0.wireOp",EDGE,"E37"),sQuery(id+"F0.wireOp",EDGE,"E38"),sQuery(id+"F0.wireOp",EDGE,"E39"),sQuery(id+"F0.wireOp",EDGE,"E40"),sQuery(id+"F0.wireOp",EDGE,"E41"),sQuery(id+"F0.wireOp",EDGE,"E42"),sQuery(id+"F0.wireOp",EDGE,"E43"),sQuery(id+"F0.wireOp",EDGE,"E44"),sQuery(id+"F0.wireOp",EDGE,"E78"),sQuery(id+"F0.wireOp",EDGE,"E79"),sQuery(id+"F0.wireOp",EDGE,"E80"),sQuery(id+"F0.wireOp",EDGE,"E81"),sQuery(id+"F0.wireOp",EDGE,"E82"),sQuery(id+"F0.wireOp",EDGE,"E83"),sQuery(id+"F0.wireOp",EDGE,"E84"),sQuery(id+"F0.wireOp",EDGE,"E85"),sQuery(id+"F0.wireOp",EDGE,"E87"),sQuery(id+"F0.wireOp",EDGE,"E88"),sQuery(id+"F0.wireOp",EDGE,"E89"),sQuery(id+"F0.wireOp",EDGE,"E90"),sQuery(id+"F0.wireOp",EDGE,"E91"),sQuery(id+"F0.wireOp",EDGE,"E92"),sQuery(id+"F0.wireOp",EDGE,"E93"),sQuery(id+"F0.wireOp",EDGE,"E94"),sQuery(id+"F0.wireOp",EDGE,"E95"),sQuery(id+"F0.wireOp",EDGE,"E96"),sQuery(id+"F0.wireOp",EDGE,"E97"),sQuery(id+"F0.wireOp",EDGE,"E98"),sQuery(id+"F0.wireOp",EDGE,"E99"),sQuery(id+"F0.wireOp",EDGE,"E100"),sQuery(id+"F0.wireOp",EDGE,"E101"),sQuery(id+"F0.wireOp",EDGE,"E102"),sQuery(id+"F0.wireOp",EDGE,"E103"),sQuery(id+"F0.wireOp",EDGE,"E104"),sQuery(id+"F0.wireOp",EDGE,"E105"),sQuery(id+"F0.wireOp",EDGE,"E106"),sQuery(id+"F0.wireOp",EDGE,"E107"),sQuery(id+"F0.wireOp",EDGE,"E108"),sQuery(id+"F0.wireOp",EDGE,"E109"),sQuery(id+"F0.wireOp",EDGE,"E110"),sQuery(id+"F0.wireOp",EDGE,"E111"),sQuery(id+"F0.wireOp",EDGE,"E112"),sQuery(id+"F0.wireOp",EDGE,"E113"),sQuery(id+"F0.wireOp",EDGE,"E114"),sQuery(id+"F0.wireOp",EDGE,"E115"),sQuery(id+"F0.wireOp",EDGE,"E116"),sQuery(id+"F0.wireOp",EDGE,"E117"),sQuery(id+"F0.wireOp",EDGE,"E118"),sQuery(id+"F0.wireOp",EDGE,"E119"),sQuery(id+"F0.wireOp",EDGE,"E120"),sQuery(id+"F0.wireOp",EDGE,"E121"),sQuery(id+"F0.wireOp",EDGE,"E122"),sQuery(id+"F0.wireOp",EDGE,"E123"),sQuery(id+"F0.wireOp",EDGE,"E124"),sQuery(id+"F0.wireOp",EDGE,"E125"),sQuery(id+"F0.wireOp",EDGE,"E126"),sQuery(id+"F0.wireOp",EDGE,"E127"),sQuery(id+"F0.wireOp",EDGE,"E128"),sQuery(id+"F0.wireOp",EDGE,"E129"),sQuery(id+"F0.wireOp",EDGE,"E130")])]}),"instanceName":"1"});
            transform(context, id + "F3", {"entities" : qUnion([Q0, Q1]), "transformType" : TransformType.TRANSLATION_3D, "dx" : -740 * mm, "dy" : 0 * mm, "dz" : 0 * mm, "makeCopy" : true});
        }
        {
            var Q0;
            Q0=qCreatedBy(makeId("Right.planeOp"),FACE);
            var sketch = newSketch(context, id + "F4", { "sketchPlane" : qUnion([Q0])});
            skLineSegment(sketch, "E131", {"start": v(-2.6, 15.3) * mm, "end": v(32.7, 15.3) * mm});
            skLineSegment(sketch, "E132", {"start": v(15, 32.6) * mm, "end": v(15, -1.5) * mm});
            skLineSegment(sketch, "E133", {"start": v(19.2, 25.3) * mm, "end": v(32.7, 25.3) * mm});
            skLineSegment(sketch, "E134", {"start": v(25, 32.6) * mm, "end": v(25, 19.2) * mm});
            skLineSegment(sketch, "E135", {"start": v(10.8, 25.3) * mm, "end": v(-2.7, 25.3) * mm});
            skLineSegment(sketch, "E136", {"start": v(5, 32.6) * mm, "end": v(5, 19.2) * mm});
            skLineSegment(sketch, "E137", {"start": v(19.2, 5.3) * mm, "end": v(32.7, 5.3) * mm});
            skLineSegment(sketch, "E138", {"start": v(10.8, 5.3) * mm, "end": v(-2.7, 5.3) * mm});
            skLineSegment(sketch, "E139", {"start": v(5, -2) * mm, "end": v(5, 11.4) * mm});
            skLineSegment(sketch, "E140", {"start": v(18.15, 30.3) * mm, "end": v(18.15, 27.8) * mm});
            skLineSegment(sketch, "E141", {"start": v(20.15, 27.8) * mm, "end": v(20.15, 21.85) * mm});
            skLineSegment(sketch, "E142", {"start": v(18.15, 27.8) * mm, "end": v(20.15, 27.8) * mm});
            skLineSegment(sketch, "E143", {"start": v(11.85, 30.3) * mm, "end": v(11.85, 27.8) * mm});
            skLineSegment(sketch, "E144", {"start": v(11.85, 27.8) * mm, "end": v(9.85, 27.8) * mm});
            skLineSegment(sketch, "E145", {"start": v(9.85, 27.8) * mm, "end": v(9.85, 21.85) * mm});
            skLineSegment(sketch, "E146", {"start": v(0, 18.45) * mm, "end": v(2.5, 18.45) * mm});
            skLineSegment(sketch, "E147", {"start": v(2.5, 20.45) * mm, "end": v(8.45, 20.45) * mm});
            skLineSegment(sketch, "E148", {"start": v(2.5, 18.45) * mm, "end": v(2.5, 20.45) * mm});
            skLineSegment(sketch, "E149", {"start": v(0, 12.15) * mm, "end": v(2.5, 12.15) * mm});
            skLineSegment(sketch, "E150", {"start": v(2.5, 12.15) * mm, "end": v(2.5, 10.15) * mm});
            skLineSegment(sketch, "E151", {"start": v(2.5, 10.15) * mm, "end": v(8.45, 10.15) * mm});
            skLineSegment(sketch, "E152", {"start": v(11.85, 0.3) * mm, "end": v(11.85, 2.8) * mm});
            skLineSegment(sketch, "E153", {"start": v(9.85, 2.8) * mm, "end": v(9.85, 8.75) * mm});
            skLineSegment(sketch, "E154", {"start": v(11.85, 2.8) * mm, "end": v(9.85, 2.8) * mm});
            skLineSegment(sketch, "E155", {"start": v(18.15, 0.3) * mm, "end": v(18.15, 2.8) * mm});
            skLineSegment(sketch, "E156", {"start": v(18.15, 2.8) * mm, "end": v(20.15, 2.8) * mm});
            skLineSegment(sketch, "E157", {"start": v(20.15, 2.8) * mm, "end": v(20.15, 8.75) * mm});
            skLineSegment(sketch, "E158", {"start": v(30, 12.15) * mm, "end": v(27.5, 12.15) * mm});
            skLineSegment(sketch, "E159", {"start": v(27.5, 10.15) * mm, "end": v(21.55, 10.15) * mm});
            skLineSegment(sketch, "E160", {"start": v(27.5, 12.15) * mm, "end": v(27.5, 10.15) * mm});
            skLineSegment(sketch, "E161", {"start": v(30, 18.45) * mm, "end": v(27.5, 18.45) * mm});
            skLineSegment(sketch, "E162", {"start": v(27.5, 18.45) * mm, "end": v(27.5, 20.45) * mm});
            skLineSegment(sketch, "E163", {"start": v(27.5, 20.45) * mm, "end": v(21.55, 20.45) * mm});
            skLineSegment(sketch, "E164", {"start": v(11.85, 19.8) * mm, "end": v(11.85, 21.85) * mm});
            skLineSegment(sketch, "E165", {"start": v(9.85, 21.85) * mm, "end": v(11.85, 21.85) * mm});
            skLineSegment(sketch, "E166", {"start": v(11.85, 19.8) * mm, "end": v(20.15, 21.85) * mm});
            skLineSegment(sketch, "E167", {"start": v(10.5, 12.15) * mm, "end": v(8.45, 12.15) * mm});
            skLineSegment(sketch, "E168", {"start": v(8.45, 10.15) * mm, "end": v(8.45, 12.15) * mm});
            skLineSegment(sketch, "E169", {"start": v(10.5, 12.15) * mm, "end": v(8.45, 20.45) * mm});
            skLineSegment(sketch, "E170", {"start": v(18.15, 10.8) * mm, "end": v(18.15, 8.75) * mm});
            skLineSegment(sketch, "E171", {"start": v(20.15, 8.75) * mm, "end": v(18.15, 8.75) * mm});
            skLineSegment(sketch, "E172", {"start": v(18.15, 10.8) * mm, "end": v(9.85, 8.75) * mm});
            skLineSegment(sketch, "E173", {"start": v(19.5, 18.45) * mm, "end": v(21.55, 18.45) * mm});
            skLineSegment(sketch, "E174", {"start": v(21.55, 20.45) * mm, "end": v(21.55, 18.45) * mm});
            skLineSegment(sketch, "E175", {"start": v(19.5, 18.45) * mm, "end": v(21.55, 10.15) * mm});
            skCircle(sketch, "E176", {"center": v(15, 15.3) * mm, "radius": 2.5 * mm});
            skLineSegment(sketch, "E177", {"start": v(28, 26.54) * mm, "end": v(26.24, 28.3) * mm});
            skLineSegment(sketch, "E178", {"start": v(26.24, 28.3) * mm, "end": v(23.76, 28.3) * mm});
            skLineSegment(sketch, "E179", {"start": v(23.76, 28.3) * mm, "end": v(22, 26.54) * mm});
            skLineSegment(sketch, "E180", {"start": v(22, 26.54) * mm, "end": v(22, 24.06) * mm});
            skLineSegment(sketch, "E181", {"start": v(22, 24.06) * mm, "end": v(23.76, 22.3) * mm});
            skLineSegment(sketch, "E182", {"start": v(23.76, 22.3) * mm, "end": v(26.24, 22.3) * mm});
            skLineSegment(sketch, "E183", {"start": v(26.24, 22.3) * mm, "end": v(28, 24.06) * mm});
            skLineSegment(sketch, "E184", {"start": v(28, 24.06) * mm, "end": v(28, 26.54) * mm});
            skLineSegment(sketch, "E185", {"start": v(8, 26.54) * mm, "end": v(6.24, 28.3) * mm});
            skLineSegment(sketch, "E186", {"start": v(6.24, 28.3) * mm, "end": v(3.76, 28.3) * mm});
            skLineSegment(sketch, "E187", {"start": v(3.76, 28.3) * mm, "end": v(2, 26.54) * mm});
            skLineSegment(sketch, "E188", {"start": v(2, 26.54) * mm, "end": v(2, 24.06) * mm});
            skLineSegment(sketch, "E189", {"start": v(2, 24.06) * mm, "end": v(3.76, 22.3) * mm});
            skLineSegment(sketch, "E190", {"start": v(3.76, 22.3) * mm, "end": v(6.24, 22.3) * mm});
            skLineSegment(sketch, "E191", {"start": v(6.24, 22.3) * mm, "end": v(8, 24.06) * mm});
            skLineSegment(sketch, "E192", {"start": v(8, 24.06) * mm, "end": v(8, 26.54) * mm});
            skLineSegment(sketch, "E193", {"start": v(28, 6.54) * mm, "end": v(26.24, 8.3) * mm});
            skLineSegment(sketch, "E194", {"start": v(26.24, 8.3) * mm, "end": v(23.76, 8.3) * mm});
            skLineSegment(sketch, "E195", {"start": v(23.76, 8.3) * mm, "end": v(22, 6.54) * mm});
            skLineSegment(sketch, "E196", {"start": v(22, 6.54) * mm, "end": v(22, 4.06) * mm});
            skLineSegment(sketch, "E197", {"start": v(22, 4.06) * mm, "end": v(23.76, 2.3) * mm});
            skLineSegment(sketch, "E198", {"start": v(23.76, 2.3) * mm, "end": v(26.24, 2.3) * mm});
            skLineSegment(sketch, "E199", {"start": v(26.24, 2.3) * mm, "end": v(28, 4.06) * mm});
            skLineSegment(sketch, "E200", {"start": v(28, 4.06) * mm, "end": v(28, 6.54) * mm});
            skLineSegment(sketch, "E201", {"start": v(8, 6.54) * mm, "end": v(6.24, 8.3) * mm});
            skLineSegment(sketch, "E202", {"start": v(6.24, 8.3) * mm, "end": v(3.76, 8.3) * mm});
            skLineSegment(sketch, "E203", {"start": v(3.76, 8.3) * mm, "end": v(2, 6.54) * mm});
            skLineSegment(sketch, "E204", {"start": v(2, 6.54) * mm, "end": v(2, 4.06) * mm});
            skLineSegment(sketch, "E205", {"start": v(2, 4.06) * mm, "end": v(3.76, 2.3) * mm});
            skLineSegment(sketch, "E206", {"start": v(3.76, 2.3) * mm, "end": v(6.24, 2.3) * mm});
            skLineSegment(sketch, "E207", {"start": v(6.24, 2.3) * mm, "end": v(8, 4.06) * mm});
            skLineSegment(sketch, "E208", {"start": v(8, 4.06) * mm, "end": v(8, 6.54) * mm});
            skLineSegment(sketch, "E209", {"start": v(26.5, 30.3) * mm, "end": v(26.5, 30) * mm});
            skLineSegment(sketch, "E210", {"start": v(26.5, 30) * mm, "end": v(25, 30) * mm});
            skLineSegment(sketch, "E211", {"start": v(23.5, 30.3) * mm, "end": v(23.5, 30) * mm});
            skLineSegment(sketch, "E212", {"start": v(23.5, 30) * mm, "end": v(25, 30) * mm});
            skLineSegment(sketch, "E213", {"start": v(30, 23.8) * mm, "end": v(29.7, 23.8) * mm});
            skLineSegment(sketch, "E214", {"start": v(29.7, 23.8) * mm, "end": v(29.7, 25.3) * mm});
            skLineSegment(sketch, "E215", {"start": v(30, 26.8) * mm, "end": v(29.7, 26.8) * mm});
            skLineSegment(sketch, "E216", {"start": v(29.7, 26.8) * mm, "end": v(29.7, 25.3) * mm});
            skLineSegment(sketch, "E217", {"start": v(25, -2) * mm, "end": v(25, 11.4) * mm});
            skLineSegment(sketch, "E218", {"start": v(26.5, 0.3) * mm, "end": v(26.5, 0.6) * mm});
            skLineSegment(sketch, "E219", {"start": v(26.5, 0.6) * mm, "end": v(25, 0.6) * mm});
            skLineSegment(sketch, "E220", {"start": v(23.5, 0.3) * mm, "end": v(23.5, 0.6) * mm});
            skLineSegment(sketch, "E221", {"start": v(23.5, 0.6) * mm, "end": v(25, 0.6) * mm});
            skLineSegment(sketch, "E222", {"start": v(30, 6.8) * mm, "end": v(29.7, 6.8) * mm});
            skLineSegment(sketch, "E223", {"start": v(29.7, 6.8) * mm, "end": v(29.7, 5.3) * mm});
            skLineSegment(sketch, "E224", {"start": v(30, 3.8) * mm, "end": v(29.7, 3.8) * mm});
            skLineSegment(sketch, "E225", {"start": v(29.7, 3.8) * mm, "end": v(29.7, 5.3) * mm});
            skLineSegment(sketch, "E226", {"start": v(3.5, 30.3) * mm, "end": v(3.5, 30) * mm});
            skLineSegment(sketch, "E227", {"start": v(3.5, 30) * mm, "end": v(5, 30) * mm});
            skLineSegment(sketch, "E228", {"start": v(6.5, 30.3) * mm, "end": v(6.5, 30) * mm});
            skLineSegment(sketch, "E229", {"start": v(6.5, 30) * mm, "end": v(5, 30) * mm});
            skLineSegment(sketch, "E230", {"start": v(0, 23.8) * mm, "end": v(0.3, 23.8) * mm});
            skLineSegment(sketch, "E231", {"start": v(0.3, 23.8) * mm, "end": v(0.3, 25.3) * mm});
            skLineSegment(sketch, "E232", {"start": v(0, 26.8) * mm, "end": v(0.3, 26.8) * mm});
            skLineSegment(sketch, "E233", {"start": v(0.3, 26.8) * mm, "end": v(0.3, 25.3) * mm});
            skLineSegment(sketch, "E234", {"start": v(0, 6.8) * mm, "end": v(0.3, 6.8) * mm});
            skLineSegment(sketch, "E235", {"start": v(0.3, 6.8) * mm, "end": v(0.3, 5.3) * mm});
            skLineSegment(sketch, "E236", {"start": v(0, 3.8) * mm, "end": v(0.3, 3.8) * mm});
            skLineSegment(sketch, "E237", {"start": v(0.3, 3.8) * mm, "end": v(0.3, 5.3) * mm});
            skLineSegment(sketch, "E238", {"start": v(3.5, 0.3) * mm, "end": v(3.5, 0.6) * mm});
            skLineSegment(sketch, "E239", {"start": v(3.5, 0.6) * mm, "end": v(5, 0.6) * mm});
            skLineSegment(sketch, "E240", {"start": v(6.5, 0.3) * mm, "end": v(6.5, 0.6) * mm});
            skLineSegment(sketch, "E241", {"start": v(6.5, 0.6) * mm, "end": v(5, 0.6) * mm});
            skLineSegment(sketch, "E242", {"start": v(29, 30.3) * mm, "end": v(26.5, 30.3) * mm});
            skLineSegment(sketch, "E243", {"start": v(23.5, 30.3) * mm, "end": v(18.15, 30.3) * mm});
            skLineSegment(sketch, "E244", {"start": v(30, 18.45) * mm, "end": v(30, 23.8) * mm});
            skLineSegment(sketch, "E245", {"start": v(30, 29.3) * mm, "end": v(30, 26.8) * mm});
            skLineSegment(sketch, "E246", {"start": v(30, 1.3) * mm, "end": v(30, 3.8) * mm});
            skLineSegment(sketch, "E247", {"start": v(30, 6.8) * mm, "end": v(30, 12.15) * mm});
            skLineSegment(sketch, "E248", {"start": v(18.15, 0.3) * mm, "end": v(23.5, 0.3) * mm});
            skLineSegment(sketch, "E249", {"start": v(29, 0.3) * mm, "end": v(26.5, 0.3) * mm});
            skLineSegment(sketch, "E250", {"start": v(1, 0.3) * mm, "end": v(3.5, 0.3) * mm});
            skLineSegment(sketch, "E251", {"start": v(6.5, 0.3) * mm, "end": v(11.85, 0.3) * mm});
            skLineSegment(sketch, "E252", {"start": v(0, 12.15) * mm, "end": v(0, 6.8) * mm});
            skLineSegment(sketch, "E253", {"start": v(0, 1.3) * mm, "end": v(0, 3.8) * mm});
            skLineSegment(sketch, "E254", {"start": v(0, 29.3) * mm, "end": v(0, 26.8) * mm});
            skLineSegment(sketch, "E255", {"start": v(0, 23.8) * mm, "end": v(0, 18.45) * mm});
            skLineSegment(sketch, "E256", {"start": v(11.85, 30.3) * mm, "end": v(6.5, 30.3) * mm});
            skLineSegment(sketch, "E257", {"start": v(1, 30.3) * mm, "end": v(3.5, 30.3) * mm});
            skLineSegment(sketch, "E258", {"start": v(1, 30.3) * mm, "end": v(0, 29.3) * mm});
            skLineSegment(sketch, "E259", {"start": v(0, 1.3) * mm, "end": v(1, 0.3) * mm});
            skLineSegment(sketch, "E260", {"start": v(29, 0.3) * mm, "end": v(30, 1.3) * mm});
            skLineSegment(sketch, "E261", {"start": v(30, 29.3) * mm, "end": v(29, 30.3) * mm});
            skSolve(sketch);
        }
        {
            var Q0;
            Q0 = qSketchRegion(id + "F4", true);
            extrude(context, id + "F5", {"entities" : qUnion([Q0]), "depth" : -710 * mm, "offsetDistance" : 25 * mm});
        }
        {
            var Q0;
            Q0=makeQuery(id+"F5.opExtrude","SWEPT_BODY",BODY,{"disambiguationData":[OSD([sQuery(id+"F4.wireOp",EDGE,"E140"),sQuery(id+"F4.wireOp",EDGE,"E141"),sQuery(id+"F4.wireOp",EDGE,"E142"),sQuery(id+"F4.wireOp",EDGE,"E143"),sQuery(id+"F4.wireOp",EDGE,"E144"),sQuery(id+"F4.wireOp",EDGE,"E145"),sQuery(id+"F4.wireOp",EDGE,"E146"),sQuery(id+"F4.wireOp",EDGE,"E147"),sQuery(id+"F4.wireOp",EDGE,"E148"),sQuery(id+"F4.wireOp",EDGE,"E149"),sQuery(id+"F4.wireOp",EDGE,"E150"),sQuery(id+"F4.wireOp",EDGE,"E151"),sQuery(id+"F4.wireOp",EDGE,"E152"),sQuery(id+"F4.wireOp",EDGE,"E153"),sQuery(id+"F4.wireOp",EDGE,"E154"),sQuery(id+"F4.wireOp",EDGE,"E155"),sQuery(id+"F4.wireOp",EDGE,"E156"),sQuery(id+"F4.wireOp",EDGE,"E157"),sQuery(id+"F4.wireOp",EDGE,"E158"),sQuery(id+"F4.wireOp",EDGE,"E159"),sQuery(id+"F4.wireOp",EDGE,"E160"),sQuery(id+"F4.wireOp",EDGE,"E161"),sQuery(id+"F4.wireOp",EDGE,"E162"),sQuery(id+"F4.wireOp",EDGE,"E163"),sQuery(id+"F4.wireOp",EDGE,"E164"),sQuery(id+"F4.wireOp",EDGE,"E165"),sQuery(id+"F4.wireOp",EDGE,"E166"),sQuery(id+"F4.wireOp",EDGE,"E167"),sQuery(id+"F4.wireOp",EDGE,"E168"),sQuery(id+"F4.wireOp",EDGE,"E169"),sQuery(id+"F4.wireOp",EDGE,"E170"),sQuery(id+"F4.wireOp",EDGE,"E171"),sQuery(id+"F4.wireOp",EDGE,"E172"),sQuery(id+"F4.wireOp",EDGE,"E173"),sQuery(id+"F4.wireOp",EDGE,"E174"),sQuery(id+"F4.wireOp",EDGE,"E175"),sQuery(id+"F4.wireOp",EDGE,"E176"),sQuery(id+"F4.wireOp",EDGE,"E177"),sQuery(id+"F4.wireOp",EDGE,"E178"),sQuery(id+"F4.wireOp",EDGE,"E179"),sQuery(id+"F4.wireOp",EDGE,"E180"),sQuery(id+"F4.wireOp",EDGE,"E181"),sQuery(id+"F4.wireOp",EDGE,"E182"),sQuery(id+"F4.wireOp",EDGE,"E183"),sQuery(id+"F4.wireOp",EDGE,"E184"),sQuery(id+"F4.wireOp",EDGE,"E185"),sQuery(id+"F4.wireOp",EDGE,"E186"),sQuery(id+"F4.wireOp",EDGE,"E187"),sQuery(id+"F4.wireOp",EDGE,"E188"),sQuery(id+"F4.wireOp",EDGE,"E189"),sQuery(id+"F4.wireOp",EDGE,"E190"),sQuery(id+"F4.wireOp",EDGE,"E191"),sQuery(id+"F4.wireOp",EDGE,"E192"),sQuery(id+"F4.wireOp",EDGE,"E193"),sQuery(id+"F4.wireOp",EDGE,"E194"),sQuery(id+"F4.wireOp",EDGE,"E195"),sQuery(id+"F4.wireOp",EDGE,"E196"),sQuery(id+"F4.wireOp",EDGE,"E197"),sQuery(id+"F4.wireOp",EDGE,"E198"),sQuery(id+"F4.wireOp",EDGE,"E199"),sQuery(id+"F4.wireOp",EDGE,"E200"),sQuery(id+"F4.wireOp",EDGE,"E201"),sQuery(id+"F4.wireOp",EDGE,"E202"),sQuery(id+"F4.wireOp",EDGE,"E203"),sQuery(id+"F4.wireOp",EDGE,"E204"),sQuery(id+"F4.wireOp",EDGE,"E205"),sQuery(id+"F4.wireOp",EDGE,"E206"),sQuery(id+"F4.wireOp",EDGE,"E207"),sQuery(id+"F4.wireOp",EDGE,"E208"),sQuery(id+"F4.wireOp",EDGE,"E209"),sQuery(id+"F4.wireOp",EDGE,"E210"),sQuery(id+"F4.wireOp",EDGE,"E211"),sQuery(id+"F4.wireOp",EDGE,"E212"),sQuery(id+"F4.wireOp",EDGE,"E213"),sQuery(id+"F4.wireOp",EDGE,"E214"),sQuery(id+"F4.wireOp",EDGE,"E215"),sQuery(id+"F4.wireOp",EDGE,"E216"),sQuery(id+"F4.wireOp",EDGE,"E218"),sQuery(id+"F4.wireOp",EDGE,"E219"),sQuery(id+"F4.wireOp",EDGE,"E220"),sQuery(id+"F4.wireOp",EDGE,"E221"),sQuery(id+"F4.wireOp",EDGE,"E222"),sQuery(id+"F4.wireOp",EDGE,"E223"),sQuery(id+"F4.wireOp",EDGE,"E224"),sQuery(id+"F4.wireOp",EDGE,"E225"),sQuery(id+"F4.wireOp",EDGE,"E226"),sQuery(id+"F4.wireOp",EDGE,"E227"),sQuery(id+"F4.wireOp",EDGE,"E228"),sQuery(id+"F4.wireOp",EDGE,"E229"),sQuery(id+"F4.wireOp",EDGE,"E230"),sQuery(id+"F4.wireOp",EDGE,"E231"),sQuery(id+"F4.wireOp",EDGE,"E232"),sQuery(id+"F4.wireOp",EDGE,"E233"),sQuery(id+"F4.wireOp",EDGE,"E234"),sQuery(id+"F4.wireOp",EDGE,"E235"),sQuery(id+"F4.wireOp",EDGE,"E236"),sQuery(id+"F4.wireOp",EDGE,"E237"),sQuery(id+"F4.wireOp",EDGE,"E238"),sQuery(id+"F4.wireOp",EDGE,"E239"),sQuery(id+"F4.wireOp",EDGE,"E240"),sQuery(id+"F4.wireOp",EDGE,"E241"),sQuery(id+"F4.wireOp",EDGE,"E242"),sQuery(id+"F4.wireOp",EDGE,"E243"),sQuery(id+"F4.wireOp",EDGE,"E244"),sQuery(id+"F4.wireOp",EDGE,"E245"),sQuery(id+"F4.wireOp",EDGE,"E246"),sQuery(id+"F4.wireOp",EDGE,"E247"),sQuery(id+"F4.wireOp",EDGE,"E248"),sQuery(id+"F4.wireOp",EDGE,"E249"),sQuery(id+"F4.wireOp",EDGE,"E250"),sQuery(id+"F4.wireOp",EDGE,"E251"),sQuery(id+"F4.wireOp",EDGE,"E252"),sQuery(id+"F4.wireOp",EDGE,"E253"),sQuery(id+"F4.wireOp",EDGE,"E254"),sQuery(id+"F4.wireOp",EDGE,"E255"),sQuery(id+"F4.wireOp",EDGE,"E256"),sQuery(id+"F4.wireOp",EDGE,"E257"),sQuery(id+"F4.wireOp",EDGE,"E258"),sQuery(id+"F4.wireOp",EDGE,"E259"),sQuery(id+"F4.wireOp",EDGE,"E260"),sQuery(id+"F4.wireOp",EDGE,"E261")])]});
            transform(context, id + "F6", {"entities" : qUnion([Q0]), "transformType" : TransformType.TRANSLATION_3D, "dx" : 0 * mm, "dy" : 640 * mm, "dz" : 0 * mm, "makeCopy" : true});
        }
        {
            var Q0;
            Q0=qCreatedBy(makeId("Right.planeOp"),FACE);
            cPlane(context, id + "F7", {"entities" : qUnion([Q0]), "cplaneType" : CPlaneType.OFFSET, "offset" : 30 * mm, "width" : 150 * mm, "height" : 150 * mm});
        }
        {
            var Q0;
            Q0=qCreatedBy(id+"F7.planeOp",FACE);
            var sketch = newSketch(context, id + "F8", { "sketchPlane" : qUnion([Q0])});
            skLineSegment(sketch, "E262", {"start": v(-2.6, 485.3) * mm, "end": v(32.7, 485.3) * mm});
            skLineSegment(sketch, "E263", {"start": v(15, 502.6) * mm, "end": v(15, 468.5) * mm});
            skLineSegment(sketch, "E264", {"start": v(19.2, 495.3) * mm, "end": v(32.7, 495.3) * mm});
            skLineSegment(sketch, "E265", {"start": v(25, 502.6) * mm, "end": v(25, 489.2) * mm});
            skLineSegment(sketch, "E266", {"start": v(10.8, 495.3) * mm, "end": v(-2.7, 495.3) * mm});
            skLineSegment(sketch, "E267", {"start": v(5, 502.6) * mm, "end": v(5, 489.2) * mm});
            skLineSegment(sketch, "E268", {"start": v(19.2, 475.3) * mm, "end": v(32.7, 475.3) * mm});
            skLineSegment(sketch, "E269", {"start": v(10.8, 475.3) * mm, "end": v(-2.7, 475.3) * mm});
            skLineSegment(sketch, "E270", {"start": v(5, 468) * mm, "end": v(5, 481.4) * mm});
            skLineSegment(sketch, "E271", {"start": v(18.15, 500.3) * mm, "end": v(18.15, 497.8) * mm});
            skLineSegment(sketch, "E272", {"start": v(20.15, 497.8) * mm, "end": v(20.15, 491.85) * mm});
            skLineSegment(sketch, "E273", {"start": v(18.15, 497.8) * mm, "end": v(20.15, 497.8) * mm});
            skLineSegment(sketch, "E274", {"start": v(11.85, 500.3) * mm, "end": v(11.85, 497.8) * mm});
            skLineSegment(sketch, "E275", {"start": v(11.85, 497.8) * mm, "end": v(9.85, 497.8) * mm});
            skLineSegment(sketch, "E276", {"start": v(9.85, 497.8) * mm, "end": v(9.85, 491.85) * mm});
            skLineSegment(sketch, "E277", {"start": v(0, 488.45) * mm, "end": v(2.5, 488.45) * mm});
            skLineSegment(sketch, "E278", {"start": v(2.5, 490.45) * mm, "end": v(8.45, 490.45) * mm});
            skLineSegment(sketch, "E279", {"start": v(2.5, 488.45) * mm, "end": v(2.5, 490.45) * mm});
            skLineSegment(sketch, "E280", {"start": v(0, 482.15) * mm, "end": v(2.5, 482.15) * mm});
            skLineSegment(sketch, "E281", {"start": v(2.5, 482.15) * mm, "end": v(2.5, 480.15) * mm});
            skLineSegment(sketch, "E282", {"start": v(2.5, 480.15) * mm, "end": v(8.45, 480.15) * mm});
            skLineSegment(sketch, "E283", {"start": v(11.85, 470.3) * mm, "end": v(11.85, 472.8) * mm});
            skLineSegment(sketch, "E284", {"start": v(9.85, 472.8) * mm, "end": v(9.85, 478.75) * mm});
            skLineSegment(sketch, "E285", {"start": v(11.85, 472.8) * mm, "end": v(9.85, 472.8) * mm});
            skLineSegment(sketch, "E286", {"start": v(18.15, 470.3) * mm, "end": v(18.15, 472.8) * mm});
            skLineSegment(sketch, "E287", {"start": v(18.15, 472.8) * mm, "end": v(20.15, 472.8) * mm});
            skLineSegment(sketch, "E288", {"start": v(20.15, 472.8) * mm, "end": v(20.15, 478.75) * mm});
            skLineSegment(sketch, "E289", {"start": v(30, 482.15) * mm, "end": v(27.5, 482.15) * mm});
            skLineSegment(sketch, "E290", {"start": v(27.5, 480.15) * mm, "end": v(21.55, 480.15) * mm});
            skLineSegment(sketch, "E291", {"start": v(27.5, 482.15) * mm, "end": v(27.5, 480.15) * mm});
            skLineSegment(sketch, "E292", {"start": v(30, 488.45) * mm, "end": v(27.5, 488.45) * mm});
            skLineSegment(sketch, "E293", {"start": v(27.5, 488.45) * mm, "end": v(27.5, 490.45) * mm});
            skLineSegment(sketch, "E294", {"start": v(27.5, 490.45) * mm, "end": v(21.55, 490.45) * mm});
            skLineSegment(sketch, "E295", {"start": v(11.85, 489.8) * mm, "end": v(11.85, 491.85) * mm});
            skLineSegment(sketch, "E296", {"start": v(9.85, 491.85) * mm, "end": v(11.85, 491.85) * mm});
            skLineSegment(sketch, "E297", {"start": v(11.85, 489.8) * mm, "end": v(20.15, 491.85) * mm});
            skLineSegment(sketch, "E298", {"start": v(10.5, 482.15) * mm, "end": v(8.45, 482.15) * mm});
            skLineSegment(sketch, "E299", {"start": v(8.45, 480.15) * mm, "end": v(8.45, 482.15) * mm});
            skLineSegment(sketch, "E300", {"start": v(10.5, 482.15) * mm, "end": v(8.45, 490.45) * mm});
            skLineSegment(sketch, "E301", {"start": v(18.15, 480.8) * mm, "end": v(18.15, 478.75) * mm});
            skLineSegment(sketch, "E302", {"start": v(20.15, 478.75) * mm, "end": v(18.15, 478.75) * mm});
            skLineSegment(sketch, "E303", {"start": v(18.15, 480.8) * mm, "end": v(9.85, 478.75) * mm});
            skLineSegment(sketch, "E304", {"start": v(19.5, 488.45) * mm, "end": v(21.55, 488.45) * mm});
            skLineSegment(sketch, "E305", {"start": v(21.55, 490.45) * mm, "end": v(21.55, 488.45) * mm});
            skLineSegment(sketch, "E306", {"start": v(19.5, 488.45) * mm, "end": v(21.55, 480.15) * mm});
            skCircle(sketch, "E307", {"center": v(15, 485.3) * mm, "radius": 2.5 * mm});
            skLineSegment(sketch, "E308", {"start": v(28, 496.54) * mm, "end": v(26.24, 498.3) * mm});
            skLineSegment(sketch, "E309", {"start": v(26.24, 498.3) * mm, "end": v(23.76, 498.3) * mm});
            skLineSegment(sketch, "E310", {"start": v(23.76, 498.3) * mm, "end": v(22, 496.54) * mm});
            skLineSegment(sketch, "E311", {"start": v(22, 496.54) * mm, "end": v(22, 494.06) * mm});
            skLineSegment(sketch, "E312", {"start": v(22, 494.06) * mm, "end": v(23.76, 492.3) * mm});
            skLineSegment(sketch, "E313", {"start": v(23.76, 492.3) * mm, "end": v(26.24, 492.3) * mm});
            skLineSegment(sketch, "E314", {"start": v(26.24, 492.3) * mm, "end": v(28, 494.06) * mm});
            skLineSegment(sketch, "E315", {"start": v(28, 494.06) * mm, "end": v(28, 496.54) * mm});
            skLineSegment(sketch, "E316", {"start": v(8, 496.54) * mm, "end": v(6.24, 498.3) * mm});
            skLineSegment(sketch, "E317", {"start": v(6.24, 498.3) * mm, "end": v(3.76, 498.3) * mm});
            skLineSegment(sketch, "E318", {"start": v(3.76, 498.3) * mm, "end": v(2, 496.54) * mm});
            skLineSegment(sketch, "E319", {"start": v(2, 496.54) * mm, "end": v(2, 494.06) * mm});
            skLineSegment(sketch, "E320", {"start": v(2, 494.06) * mm, "end": v(3.76, 492.3) * mm});
            skLineSegment(sketch, "E321", {"start": v(3.76, 492.3) * mm, "end": v(6.24, 492.3) * mm});
            skLineSegment(sketch, "E322", {"start": v(6.24, 492.3) * mm, "end": v(8, 494.06) * mm});
            skLineSegment(sketch, "E323", {"start": v(8, 494.06) * mm, "end": v(8, 496.54) * mm});
            skLineSegment(sketch, "E324", {"start": v(28, 476.54) * mm, "end": v(26.24, 478.3) * mm});
            skLineSegment(sketch, "E325", {"start": v(26.24, 478.3) * mm, "end": v(23.76, 478.3) * mm});
            skLineSegment(sketch, "E326", {"start": v(23.76, 478.3) * mm, "end": v(22, 476.54) * mm});
            skLineSegment(sketch, "E327", {"start": v(22, 476.54) * mm, "end": v(22, 474.06) * mm});
            skLineSegment(sketch, "E328", {"start": v(22, 474.06) * mm, "end": v(23.76, 472.3) * mm});
            skLineSegment(sketch, "E329", {"start": v(23.76, 472.3) * mm, "end": v(26.24, 472.3) * mm});
            skLineSegment(sketch, "E330", {"start": v(26.24, 472.3) * mm, "end": v(28, 474.06) * mm});
            skLineSegment(sketch, "E331", {"start": v(28, 474.06) * mm, "end": v(28, 476.54) * mm});
            skLineSegment(sketch, "E332", {"start": v(8, 476.54) * mm, "end": v(6.24, 478.3) * mm});
            skLineSegment(sketch, "E333", {"start": v(6.24, 478.3) * mm, "end": v(3.76, 478.3) * mm});
            skLineSegment(sketch, "E334", {"start": v(3.76, 478.3) * mm, "end": v(2, 476.54) * mm});
            skLineSegment(sketch, "E335", {"start": v(2, 476.54) * mm, "end": v(2, 474.06) * mm});
            skLineSegment(sketch, "E336", {"start": v(2, 474.06) * mm, "end": v(3.76, 472.3) * mm});
            skLineSegment(sketch, "E337", {"start": v(3.76, 472.3) * mm, "end": v(6.24, 472.3) * mm});
            skLineSegment(sketch, "E338", {"start": v(6.24, 472.3) * mm, "end": v(8, 474.06) * mm});
            skLineSegment(sketch, "E339", {"start": v(8, 474.06) * mm, "end": v(8, 476.54) * mm});
            skLineSegment(sketch, "E340", {"start": v(26.5, 500.3) * mm, "end": v(26.5, 500) * mm});
            skLineSegment(sketch, "E341", {"start": v(26.5, 500) * mm, "end": v(25, 500) * mm});
            skLineSegment(sketch, "E342", {"start": v(23.5, 500.3) * mm, "end": v(23.5, 500) * mm});
            skLineSegment(sketch, "E343", {"start": v(23.5, 500) * mm, "end": v(25, 500) * mm});
            skLineSegment(sketch, "E344", {"start": v(30, 493.8) * mm, "end": v(29.7, 493.8) * mm});
            skLineSegment(sketch, "E345", {"start": v(29.7, 493.8) * mm, "end": v(29.7, 495.3) * mm});
            skLineSegment(sketch, "E346", {"start": v(30, 496.8) * mm, "end": v(29.7, 496.8) * mm});
            skLineSegment(sketch, "E347", {"start": v(29.7, 496.8) * mm, "end": v(29.7, 495.3) * mm});
            skLineSegment(sketch, "E348", {"start": v(25, 468) * mm, "end": v(25, 481.4) * mm});
            skLineSegment(sketch, "E349", {"start": v(26.5, 470.3) * mm, "end": v(26.5, 470.6) * mm});
            skLineSegment(sketch, "E350", {"start": v(26.5, 470.6) * mm, "end": v(25, 470.6) * mm});
            skLineSegment(sketch, "E351", {"start": v(23.5, 470.3) * mm, "end": v(23.5, 470.6) * mm});
            skLineSegment(sketch, "E352", {"start": v(23.5, 470.6) * mm, "end": v(25, 470.6) * mm});
            skLineSegment(sketch, "E353", {"start": v(30, 476.8) * mm, "end": v(29.7, 476.8) * mm});
            skLineSegment(sketch, "E354", {"start": v(29.7, 476.8) * mm, "end": v(29.7, 475.3) * mm});
            skLineSegment(sketch, "E355", {"start": v(30, 473.8) * mm, "end": v(29.7, 473.8) * mm});
            skLineSegment(sketch, "E356", {"start": v(29.7, 473.8) * mm, "end": v(29.7, 475.3) * mm});
            skLineSegment(sketch, "E357", {"start": v(3.5, 500.3) * mm, "end": v(3.5, 500) * mm});
            skLineSegment(sketch, "E358", {"start": v(3.5, 500) * mm, "end": v(5, 500) * mm});
            skLineSegment(sketch, "E359", {"start": v(6.5, 500.3) * mm, "end": v(6.5, 500) * mm});
            skLineSegment(sketch, "E360", {"start": v(6.5, 500) * mm, "end": v(5, 500) * mm});
            skLineSegment(sketch, "E361", {"start": v(0, 493.8) * mm, "end": v(0.3, 493.8) * mm});
            skLineSegment(sketch, "E362", {"start": v(0.3, 493.8) * mm, "end": v(0.3, 495.3) * mm});
            skLineSegment(sketch, "E363", {"start": v(0, 496.8) * mm, "end": v(0.3, 496.8) * mm});
            skLineSegment(sketch, "E364", {"start": v(0.3, 496.8) * mm, "end": v(0.3, 495.3) * mm});
            skLineSegment(sketch, "E365", {"start": v(0, 476.8) * mm, "end": v(0.3, 476.8) * mm});
            skLineSegment(sketch, "E366", {"start": v(0.3, 476.8) * mm, "end": v(0.3, 475.3) * mm});
            skLineSegment(sketch, "E367", {"start": v(0, 473.8) * mm, "end": v(0.3, 473.8) * mm});
            skLineSegment(sketch, "E368", {"start": v(0.3, 473.8) * mm, "end": v(0.3, 475.3) * mm});
            skLineSegment(sketch, "E369", {"start": v(3.5, 470.3) * mm, "end": v(3.5, 470.6) * mm});
            skLineSegment(sketch, "E370", {"start": v(3.5, 470.6) * mm, "end": v(5, 470.6) * mm});
            skLineSegment(sketch, "E371", {"start": v(6.5, 470.3) * mm, "end": v(6.5, 470.6) * mm});
            skLineSegment(sketch, "E372", {"start": v(6.5, 470.6) * mm, "end": v(5, 470.6) * mm});
            skLineSegment(sketch, "E373", {"start": v(29, 500.3) * mm, "end": v(26.5, 500.3) * mm});
            skLineSegment(sketch, "E374", {"start": v(23.5, 500.3) * mm, "end": v(18.15, 500.3) * mm});
            skLineSegment(sketch, "E375", {"start": v(30, 488.45) * mm, "end": v(30, 493.8) * mm});
            skLineSegment(sketch, "E376", {"start": v(30, 499.3) * mm, "end": v(30, 496.8) * mm});
            skLineSegment(sketch, "E377", {"start": v(30, 471.3) * mm, "end": v(30, 473.8) * mm});
            skLineSegment(sketch, "E378", {"start": v(30, 476.8) * mm, "end": v(30, 482.15) * mm});
            skLineSegment(sketch, "E379", {"start": v(18.15, 470.3) * mm, "end": v(23.5, 470.3) * mm});
            skLineSegment(sketch, "E380", {"start": v(29, 470.3) * mm, "end": v(26.5, 470.3) * mm});
            skLineSegment(sketch, "E381", {"start": v(1, 470.3) * mm, "end": v(3.5, 470.3) * mm});
            skLineSegment(sketch, "E382", {"start": v(6.5, 470.3) * mm, "end": v(11.85, 470.3) * mm});
            skLineSegment(sketch, "E383", {"start": v(0, 482.15) * mm, "end": v(0, 476.8) * mm});
            skLineSegment(sketch, "E384", {"start": v(0, 471.3) * mm, "end": v(0, 473.8) * mm});
            skLineSegment(sketch, "E385", {"start": v(0, 499.3) * mm, "end": v(0, 496.8) * mm});
            skLineSegment(sketch, "E386", {"start": v(0, 493.8) * mm, "end": v(0, 488.45) * mm});
            skLineSegment(sketch, "E387", {"start": v(11.85, 500.3) * mm, "end": v(6.5, 500.3) * mm});
            skLineSegment(sketch, "E388", {"start": v(1, 500.3) * mm, "end": v(3.5, 500.3) * mm});
            skLineSegment(sketch, "E389", {"start": v(1, 500.3) * mm, "end": v(0, 499.3) * mm});
            skLineSegment(sketch, "E390", {"start": v(0, 471.3) * mm, "end": v(1, 470.3) * mm});
            skLineSegment(sketch, "E391", {"start": v(29, 470.3) * mm, "end": v(30, 471.3) * mm});
            skLineSegment(sketch, "E392", {"start": v(30, 499.3) * mm, "end": v(29, 500.3) * mm});
            skSolve(sketch);
        }
        {
            var Q0;
            Q0 = qSketchRegion(id + "F8", true);
            extrude(context, id + "F9", {"entities" : qUnion([Q0]), "depth" : -770 * mm, "offsetDistance" : 25 * mm});
        }
        {
            var Q0;
            Q0=makeQuery(id+"F9.opExtrude","SWEPT_BODY",BODY,{"disambiguationData":[OSD([sQuery(id+"F8.wireOp",EDGE,"E271"),sQuery(id+"F8.wireOp",EDGE,"E272"),sQuery(id+"F8.wireOp",EDGE,"E273"),sQuery(id+"F8.wireOp",EDGE,"E274"),sQuery(id+"F8.wireOp",EDGE,"E275"),sQuery(id+"F8.wireOp",EDGE,"E276"),sQuery(id+"F8.wireOp",EDGE,"E277"),sQuery(id+"F8.wireOp",EDGE,"E278"),sQuery(id+"F8.wireOp",EDGE,"E279"),sQuery(id+"F8.wireOp",EDGE,"E280"),sQuery(id+"F8.wireOp",EDGE,"E281"),sQuery(id+"F8.wireOp",EDGE,"E282"),sQuery(id+"F8.wireOp",EDGE,"E283"),sQuery(id+"F8.wireOp",EDGE,"E284"),sQuery(id+"F8.wireOp",EDGE,"E285"),sQuery(id+"F8.wireOp",EDGE,"E286"),sQuery(id+"F8.wireOp",EDGE,"E287"),sQuery(id+"F8.wireOp",EDGE,"E288"),sQuery(id+"F8.wireOp",EDGE,"E289"),sQuery(id+"F8.wireOp",EDGE,"E290"),sQuery(id+"F8.wireOp",EDGE,"E291"),sQuery(id+"F8.wireOp",EDGE,"E292"),sQuery(id+"F8.wireOp",EDGE,"E293"),sQuery(id+"F8.wireOp",EDGE,"E294"),sQuery(id+"F8.wireOp",EDGE,"E295"),sQuery(id+"F8.wireOp",EDGE,"E296"),sQuery(id+"F8.wireOp",EDGE,"E297"),sQuery(id+"F8.wireOp",EDGE,"E298"),sQuery(id+"F8.wireOp",EDGE,"E299"),sQuery(id+"F8.wireOp",EDGE,"E300"),sQuery(id+"F8.wireOp",EDGE,"E301"),sQuery(id+"F8.wireOp",EDGE,"E302"),sQuery(id+"F8.wireOp",EDGE,"E303"),sQuery(id+"F8.wireOp",EDGE,"E304"),sQuery(id+"F8.wireOp",EDGE,"E305"),sQuery(id+"F8.wireOp",EDGE,"E306"),sQuery(id+"F8.wireOp",EDGE,"E307"),sQuery(id+"F8.wireOp",EDGE,"E308"),sQuery(id+"F8.wireOp",EDGE,"E309"),sQuery(id+"F8.wireOp",EDGE,"E310"),sQuery(id+"F8.wireOp",EDGE,"E311"),sQuery(id+"F8.wireOp",EDGE,"E312"),sQuery(id+"F8.wireOp",EDGE,"E313"),sQuery(id+"F8.wireOp",EDGE,"E314"),sQuery(id+"F8.wireOp",EDGE,"E315"),sQuery(id+"F8.wireOp",EDGE,"E316"),sQuery(id+"F8.wireOp",EDGE,"E317"),sQuery(id+"F8.wireOp",EDGE,"E318"),sQuery(id+"F8.wireOp",EDGE,"E319"),sQuery(id+"F8.wireOp",EDGE,"E320"),sQuery(id+"F8.wireOp",EDGE,"E321"),sQuery(id+"F8.wireOp",EDGE,"E322"),sQuery(id+"F8.wireOp",EDGE,"E323"),sQuery(id+"F8.wireOp",EDGE,"E324"),sQuery(id+"F8.wireOp",EDGE,"E325"),sQuery(id+"F8.wireOp",EDGE,"E326"),sQuery(id+"F8.wireOp",EDGE,"E327"),sQuery(id+"F8.wireOp",EDGE,"E328"),sQuery(id+"F8.wireOp",EDGE,"E329"),sQuery(id+"F8.wireOp",EDGE,"E330"),sQuery(id+"F8.wireOp",EDGE,"E331"),sQuery(id+"F8.wireOp",EDGE,"E332"),sQuery(id+"F8.wireOp",EDGE,"E333"),sQuery(id+"F8.wireOp",EDGE,"E334"),sQuery(id+"F8.wireOp",EDGE,"E335"),sQuery(id+"F8.wireOp",EDGE,"E336"),sQuery(id+"F8.wireOp",EDGE,"E337"),sQuery(id+"F8.wireOp",EDGE,"E338"),sQuery(id+"F8.wireOp",EDGE,"E339"),sQuery(id+"F8.wireOp",EDGE,"E340"),sQuery(id+"F8.wireOp",EDGE,"E341"),sQuery(id+"F8.wireOp",EDGE,"E342"),sQuery(id+"F8.wireOp",EDGE,"E343"),sQuery(id+"F8.wireOp",EDGE,"E344"),sQuery(id+"F8.wireOp",EDGE,"E345"),sQuery(id+"F8.wireOp",EDGE,"E346"),sQuery(id+"F8.wireOp",EDGE,"E347"),sQuery(id+"F8.wireOp",EDGE,"E349"),sQuery(id+"F8.wireOp",EDGE,"E350"),sQuery(id+"F8.wireOp",EDGE,"E351"),sQuery(id+"F8.wireOp",EDGE,"E352"),sQuery(id+"F8.wireOp",EDGE,"E353"),sQuery(id+"F8.wireOp",EDGE,"E354"),sQuery(id+"F8.wireOp",EDGE,"E355"),sQuery(id+"F8.wireOp",EDGE,"E356"),sQuery(id+"F8.wireOp",EDGE,"E357"),sQuery(id+"F8.wireOp",EDGE,"E358"),sQuery(id+"F8.wireOp",EDGE,"E359"),sQuery(id+"F8.wireOp",EDGE,"E360"),sQuery(id+"F8.wireOp",EDGE,"E361"),sQuery(id+"F8.wireOp",EDGE,"E362"),sQuery(id+"F8.wireOp",EDGE,"E363"),sQuery(id+"F8.wireOp",EDGE,"E364"),sQuery(id+"F8.wireOp",EDGE,"E365"),sQuery(id+"F8.wireOp",EDGE,"E366"),sQuery(id+"F8.wireOp",EDGE,"E367"),sQuery(id+"F8.wireOp",EDGE,"E368"),sQuery(id+"F8.wireOp",EDGE,"E369"),sQuery(id+"F8.wireOp",EDGE,"E370"),sQuery(id+"F8.wireOp",EDGE,"E371"),sQuery(id+"F8.wireOp",EDGE,"E372"),sQuery(id+"F8.wireOp",EDGE,"E373"),sQuery(id+"F8.wireOp",EDGE,"E374"),sQuery(id+"F8.wireOp",EDGE,"E375"),sQuery(id+"F8.wireOp",EDGE,"E376"),sQuery(id+"F8.wireOp",EDGE,"E377"),sQuery(id+"F8.wireOp",EDGE,"E378"),sQuery(id+"F8.wireOp",EDGE,"E379"),sQuery(id+"F8.wireOp",EDGE,"E380"),sQuery(id+"F8.wireOp",EDGE,"E381"),sQuery(id+"F8.wireOp",EDGE,"E382"),sQuery(id+"F8.wireOp",EDGE,"E383"),sQuery(id+"F8.wireOp",EDGE,"E384"),sQuery(id+"F8.wireOp",EDGE,"E385"),sQuery(id+"F8.wireOp",EDGE,"E386"),sQuery(id+"F8.wireOp",EDGE,"E387"),sQuery(id+"F8.wireOp",EDGE,"E388"),sQuery(id+"F8.wireOp",EDGE,"E389"),sQuery(id+"F8.wireOp",EDGE,"E390"),sQuery(id+"F8.wireOp",EDGE,"E391"),sQuery(id+"F8.wireOp",EDGE,"E392")])]});
            transform(context, id + "F10", {"entities" : qUnion([Q0]), "transformType" : TransformType.TRANSLATION_3D, "dx" : 0 * mm, "dy" : 640 * mm, "dz" : 0 * mm, "makeCopy" : true});
        }
        {
            var Q0;
            Q0=qCreatedBy(makeId("Front.planeOp"),FACE);
            cPlane(context, id + "F11", {"entities" : qUnion([Q0]), "cplaneType" : CPlaneType.OFFSET, "offset" : 30 * mm, "oppositeDirection" : true, "width" : 150 * mm, "height" : 150 * mm});
        }
        {
            var Q0;
            Q0=qCreatedBy(id+"F11.planeOp",FACE);
            var sketch = newSketch(context, id + "F12", { "sketchPlane" : qUnion([Q0])});
            skLineSegment(sketch, "E393", {"start": v(-2.6, 15.3) * mm, "end": v(32.7, 15.3) * mm});
            skLineSegment(sketch, "E394", {"start": v(15, 32.6) * mm, "end": v(15, -1.5) * mm});
            skLineSegment(sketch, "E395", {"start": v(19.2, 25.3) * mm, "end": v(32.7, 25.3) * mm});
            skLineSegment(sketch, "E396", {"start": v(25, 32.6) * mm, "end": v(25, 19.2) * mm});
            skLineSegment(sketch, "E397", {"start": v(10.8, 25.3) * mm, "end": v(-2.7, 25.3) * mm});
            skLineSegment(sketch, "E398", {"start": v(5, 32.6) * mm, "end": v(5, 19.2) * mm});
            skLineSegment(sketch, "E399", {"start": v(19.2, 5.3) * mm, "end": v(32.7, 5.3) * mm});
            skLineSegment(sketch, "E400", {"start": v(10.8, 5.3) * mm, "end": v(-2.7, 5.3) * mm});
            skLineSegment(sketch, "E401", {"start": v(5, -2) * mm, "end": v(5, 11.4) * mm});
            skLineSegment(sketch, "E402", {"start": v(18.15, 30.3) * mm, "end": v(18.15, 27.8) * mm});
            skLineSegment(sketch, "E403", {"start": v(20.15, 27.8) * mm, "end": v(20.15, 21.85) * mm});
            skLineSegment(sketch, "E404", {"start": v(18.15, 27.8) * mm, "end": v(20.15, 27.8) * mm});
            skLineSegment(sketch, "E405", {"start": v(11.85, 30.3) * mm, "end": v(11.85, 27.8) * mm});
            skLineSegment(sketch, "E406", {"start": v(11.85, 27.8) * mm, "end": v(9.85, 27.8) * mm});
            skLineSegment(sketch, "E407", {"start": v(9.85, 27.8) * mm, "end": v(9.85, 21.85) * mm});
            skLineSegment(sketch, "E408", {"start": v(0, 18.45) * mm, "end": v(2.5, 18.45) * mm});
            skLineSegment(sketch, "E409", {"start": v(2.5, 20.45) * mm, "end": v(8.45, 20.45) * mm});
            skLineSegment(sketch, "E410", {"start": v(2.5, 18.45) * mm, "end": v(2.5, 20.45) * mm});
            skLineSegment(sketch, "E411", {"start": v(0, 12.15) * mm, "end": v(2.5, 12.15) * mm});
            skLineSegment(sketch, "E412", {"start": v(2.5, 12.15) * mm, "end": v(2.5, 10.15) * mm});
            skLineSegment(sketch, "E413", {"start": v(2.5, 10.15) * mm, "end": v(8.45, 10.15) * mm});
            skLineSegment(sketch, "E414", {"start": v(11.85, 0.3) * mm, "end": v(11.85, 2.8) * mm});
            skLineSegment(sketch, "E415", {"start": v(9.85, 2.8) * mm, "end": v(9.85, 8.75) * mm});
            skLineSegment(sketch, "E416", {"start": v(11.85, 2.8) * mm, "end": v(9.85, 2.8) * mm});
            skLineSegment(sketch, "E417", {"start": v(18.15, 0.3) * mm, "end": v(18.15, 2.8) * mm});
            skLineSegment(sketch, "E418", {"start": v(18.15, 2.8) * mm, "end": v(20.15, 2.8) * mm});
            skLineSegment(sketch, "E419", {"start": v(20.15, 2.8) * mm, "end": v(20.15, 8.75) * mm});
            skLineSegment(sketch, "E420", {"start": v(30, 12.15) * mm, "end": v(27.5, 12.15) * mm});
            skLineSegment(sketch, "E421", {"start": v(27.5, 10.15) * mm, "end": v(21.55, 10.15) * mm});
            skLineSegment(sketch, "E422", {"start": v(27.5, 12.15) * mm, "end": v(27.5, 10.15) * mm});
            skLineSegment(sketch, "E423", {"start": v(30, 18.45) * mm, "end": v(27.5, 18.45) * mm});
            skLineSegment(sketch, "E424", {"start": v(27.5, 18.45) * mm, "end": v(27.5, 20.45) * mm});
            skLineSegment(sketch, "E425", {"start": v(27.5, 20.45) * mm, "end": v(21.55, 20.45) * mm});
            skLineSegment(sketch, "E426", {"start": v(11.85, 19.8) * mm, "end": v(11.85, 21.85) * mm});
            skLineSegment(sketch, "E427", {"start": v(9.85, 21.85) * mm, "end": v(11.85, 21.85) * mm});
            skLineSegment(sketch, "E428", {"start": v(11.85, 19.8) * mm, "end": v(20.15, 21.85) * mm});
            skLineSegment(sketch, "E429", {"start": v(10.5, 12.15) * mm, "end": v(8.45, 12.15) * mm});
            skLineSegment(sketch, "E430", {"start": v(8.45, 10.15) * mm, "end": v(8.45, 12.15) * mm});
            skLineSegment(sketch, "E431", {"start": v(10.5, 12.15) * mm, "end": v(8.45, 20.45) * mm});
            skLineSegment(sketch, "E432", {"start": v(18.15, 10.8) * mm, "end": v(18.15, 8.75) * mm});
            skLineSegment(sketch, "E433", {"start": v(20.15, 8.75) * mm, "end": v(18.15, 8.75) * mm});
            skLineSegment(sketch, "E434", {"start": v(18.15, 10.8) * mm, "end": v(9.85, 8.75) * mm});
            skLineSegment(sketch, "E435", {"start": v(19.5, 18.45) * mm, "end": v(21.55, 18.45) * mm});
            skLineSegment(sketch, "E436", {"start": v(21.55, 20.45) * mm, "end": v(21.55, 18.45) * mm});
            skLineSegment(sketch, "E437", {"start": v(19.5, 18.45) * mm, "end": v(21.55, 10.15) * mm});
            skCircle(sketch, "E438", {"center": v(15, 15.3) * mm, "radius": 2.5 * mm});
            skLineSegment(sketch, "E439", {"start": v(28, 26.54) * mm, "end": v(26.24, 28.3) * mm});
            skLineSegment(sketch, "E440", {"start": v(26.24, 28.3) * mm, "end": v(23.76, 28.3) * mm});
            skLineSegment(sketch, "E441", {"start": v(23.76, 28.3) * mm, "end": v(22, 26.54) * mm});
            skLineSegment(sketch, "E442", {"start": v(22, 26.54) * mm, "end": v(22, 24.06) * mm});
            skLineSegment(sketch, "E443", {"start": v(22, 24.06) * mm, "end": v(23.76, 22.3) * mm});
            skLineSegment(sketch, "E444", {"start": v(23.76, 22.3) * mm, "end": v(26.24, 22.3) * mm});
            skLineSegment(sketch, "E445", {"start": v(26.24, 22.3) * mm, "end": v(28, 24.06) * mm});
            skLineSegment(sketch, "E446", {"start": v(28, 24.06) * mm, "end": v(28, 26.54) * mm});
            skLineSegment(sketch, "E447", {"start": v(8, 26.54) * mm, "end": v(6.24, 28.3) * mm});
            skLineSegment(sketch, "E448", {"start": v(6.24, 28.3) * mm, "end": v(3.76, 28.3) * mm});
            skLineSegment(sketch, "E449", {"start": v(3.76, 28.3) * mm, "end": v(2, 26.54) * mm});
            skLineSegment(sketch, "E450", {"start": v(2, 26.54) * mm, "end": v(2, 24.06) * mm});
            skLineSegment(sketch, "E451", {"start": v(2, 24.06) * mm, "end": v(3.76, 22.3) * mm});
            skLineSegment(sketch, "E452", {"start": v(3.76, 22.3) * mm, "end": v(6.24, 22.3) * mm});
            skLineSegment(sketch, "E453", {"start": v(6.24, 22.3) * mm, "end": v(8, 24.06) * mm});
            skLineSegment(sketch, "E454", {"start": v(8, 24.06) * mm, "end": v(8, 26.54) * mm});
            skLineSegment(sketch, "E455", {"start": v(28, 6.54) * mm, "end": v(26.24, 8.3) * mm});
            skLineSegment(sketch, "E456", {"start": v(26.24, 8.3) * mm, "end": v(23.76, 8.3) * mm});
            skLineSegment(sketch, "E457", {"start": v(23.76, 8.3) * mm, "end": v(22, 6.54) * mm});
            skLineSegment(sketch, "E458", {"start": v(22, 6.54) * mm, "end": v(22, 4.06) * mm});
            skLineSegment(sketch, "E459", {"start": v(22, 4.06) * mm, "end": v(23.76, 2.3) * mm});
            skLineSegment(sketch, "E460", {"start": v(23.76, 2.3) * mm, "end": v(26.24, 2.3) * mm});
            skLineSegment(sketch, "E461", {"start": v(26.24, 2.3) * mm, "end": v(28, 4.06) * mm});
            skLineSegment(sketch, "E462", {"start": v(28, 4.06) * mm, "end": v(28, 6.54) * mm});
            skLineSegment(sketch, "E463", {"start": v(8, 6.54) * mm, "end": v(6.24, 8.3) * mm});
            skLineSegment(sketch, "E464", {"start": v(6.24, 8.3) * mm, "end": v(3.76, 8.3) * mm});
            skLineSegment(sketch, "E465", {"start": v(3.76, 8.3) * mm, "end": v(2, 6.54) * mm});
            skLineSegment(sketch, "E466", {"start": v(2, 6.54) * mm, "end": v(2, 4.06) * mm});
            skLineSegment(sketch, "E467", {"start": v(2, 4.06) * mm, "end": v(3.76, 2.3) * mm});
            skLineSegment(sketch, "E468", {"start": v(3.76, 2.3) * mm, "end": v(6.24, 2.3) * mm});
            skLineSegment(sketch, "E469", {"start": v(6.24, 2.3) * mm, "end": v(8, 4.06) * mm});
            skLineSegment(sketch, "E470", {"start": v(8, 4.06) * mm, "end": v(8, 6.54) * mm});
            skLineSegment(sketch, "E471", {"start": v(26.5, 30.3) * mm, "end": v(26.5, 30) * mm});
            skLineSegment(sketch, "E472", {"start": v(26.5, 30) * mm, "end": v(25, 30) * mm});
            skLineSegment(sketch, "E473", {"start": v(23.5, 30.3) * mm, "end": v(23.5, 30) * mm});
            skLineSegment(sketch, "E474", {"start": v(23.5, 30) * mm, "end": v(25, 30) * mm});
            skLineSegment(sketch, "E475", {"start": v(30, 23.8) * mm, "end": v(29.7, 23.8) * mm});
            skLineSegment(sketch, "E476", {"start": v(29.7, 23.8) * mm, "end": v(29.7, 25.3) * mm});
            skLineSegment(sketch, "E477", {"start": v(30, 26.8) * mm, "end": v(29.7, 26.8) * mm});
            skLineSegment(sketch, "E478", {"start": v(29.7, 26.8) * mm, "end": v(29.7, 25.3) * mm});
            skLineSegment(sketch, "E479", {"start": v(25, -2) * mm, "end": v(25, 11.4) * mm});
            skLineSegment(sketch, "E480", {"start": v(26.5, 0.3) * mm, "end": v(26.5, 0.6) * mm});
            skLineSegment(sketch, "E481", {"start": v(26.5, 0.6) * mm, "end": v(25, 0.6) * mm});
            skLineSegment(sketch, "E482", {"start": v(23.5, 0.3) * mm, "end": v(23.5, 0.6) * mm});
            skLineSegment(sketch, "E483", {"start": v(23.5, 0.6) * mm, "end": v(25, 0.6) * mm});
            skLineSegment(sketch, "E484", {"start": v(30, 6.8) * mm, "end": v(29.7, 6.8) * mm});
            skLineSegment(sketch, "E485", {"start": v(29.7, 6.8) * mm, "end": v(29.7, 5.3) * mm});
            skLineSegment(sketch, "E486", {"start": v(30, 3.8) * mm, "end": v(29.7, 3.8) * mm});
            skLineSegment(sketch, "E487", {"start": v(29.7, 3.8) * mm, "end": v(29.7, 5.3) * mm});
            skLineSegment(sketch, "E488", {"start": v(3.5, 30.3) * mm, "end": v(3.5, 30) * mm});
            skLineSegment(sketch, "E489", {"start": v(3.5, 30) * mm, "end": v(5, 30) * mm});
            skLineSegment(sketch, "E490", {"start": v(6.5, 30.3) * mm, "end": v(6.5, 30) * mm});
            skLineSegment(sketch, "E491", {"start": v(6.5, 30) * mm, "end": v(5, 30) * mm});
            skLineSegment(sketch, "E492", {"start": v(0, 23.8) * mm, "end": v(0.3, 23.8) * mm});
            skLineSegment(sketch, "E493", {"start": v(0.3, 23.8) * mm, "end": v(0.3, 25.3) * mm});
            skLineSegment(sketch, "E494", {"start": v(0, 26.8) * mm, "end": v(0.3, 26.8) * mm});
            skLineSegment(sketch, "E495", {"start": v(0.3, 26.8) * mm, "end": v(0.3, 25.3) * mm});
            skLineSegment(sketch, "E496", {"start": v(0, 6.8) * mm, "end": v(0.3, 6.8) * mm});
            skLineSegment(sketch, "E497", {"start": v(0.3, 6.8) * mm, "end": v(0.3, 5.3) * mm});
            skLineSegment(sketch, "E498", {"start": v(0, 3.8) * mm, "end": v(0.3, 3.8) * mm});
            skLineSegment(sketch, "E499", {"start": v(0.3, 3.8) * mm, "end": v(0.3, 5.3) * mm});
            skLineSegment(sketch, "E500", {"start": v(3.5, 0.3) * mm, "end": v(3.5, 0.6) * mm});
            skLineSegment(sketch, "E501", {"start": v(3.5, 0.6) * mm, "end": v(5, 0.6) * mm});
            skLineSegment(sketch, "E502", {"start": v(6.5, 0.3) * mm, "end": v(6.5, 0.6) * mm});
            skLineSegment(sketch, "E503", {"start": v(6.5, 0.6) * mm, "end": v(5, 0.6) * mm});
            skLineSegment(sketch, "E504", {"start": v(29, 30.3) * mm, "end": v(26.5, 30.3) * mm});
            skLineSegment(sketch, "E505", {"start": v(23.5, 30.3) * mm, "end": v(18.15, 30.3) * mm});
            skLineSegment(sketch, "E506", {"start": v(30, 18.45) * mm, "end": v(30, 23.8) * mm});
            skLineSegment(sketch, "E507", {"start": v(30, 29.3) * mm, "end": v(30, 26.8) * mm});
            skLineSegment(sketch, "E508", {"start": v(30, 1.3) * mm, "end": v(30, 3.8) * mm});
            skLineSegment(sketch, "E509", {"start": v(30, 6.8) * mm, "end": v(30, 12.15) * mm});
            skLineSegment(sketch, "E510", {"start": v(18.15, 0.3) * mm, "end": v(23.5, 0.3) * mm});
            skLineSegment(sketch, "E511", {"start": v(29, 0.3) * mm, "end": v(26.5, 0.3) * mm});
            skLineSegment(sketch, "E512", {"start": v(1, 0.3) * mm, "end": v(3.5, 0.3) * mm});
            skLineSegment(sketch, "E513", {"start": v(6.5, 0.3) * mm, "end": v(11.85, 0.3) * mm});
            skLineSegment(sketch, "E514", {"start": v(0, 12.15) * mm, "end": v(0, 6.8) * mm});
            skLineSegment(sketch, "E515", {"start": v(0, 1.3) * mm, "end": v(0, 3.8) * mm});
            skLineSegment(sketch, "E516", {"start": v(0, 29.3) * mm, "end": v(0, 26.8) * mm});
            skLineSegment(sketch, "E517", {"start": v(0, 23.8) * mm, "end": v(0, 18.45) * mm});
            skLineSegment(sketch, "E518", {"start": v(11.85, 30.3) * mm, "end": v(6.5, 30.3) * mm});
            skLineSegment(sketch, "E519", {"start": v(1, 30.3) * mm, "end": v(3.5, 30.3) * mm});
            skLineSegment(sketch, "E520", {"start": v(1, 30.3) * mm, "end": v(0, 29.3) * mm});
            skLineSegment(sketch, "E521", {"start": v(0, 1.3) * mm, "end": v(1, 0.3) * mm});
            skLineSegment(sketch, "E522", {"start": v(29, 0.3) * mm, "end": v(30, 1.3) * mm});
            skLineSegment(sketch, "E523", {"start": v(30, 29.3) * mm, "end": v(29, 30.3) * mm});
            skSolve(sketch);
        }
        {
            var Q0;
            Q0 = qSketchRegion(id + "F12", true);
            extrude(context, id + "F13", {"entities" : qUnion([Q0]), "oppositeDirection" : true, "depth" : 610 * mm, "offsetDistance" : 25 * mm});
        }
        {
            var Q0;
            Q0=makeQuery(id+"F13.opExtrude","SWEPT_BODY",BODY,{"disambiguationData":[OSD([sQuery(id+"F12.wireOp",EDGE,"E402"),sQuery(id+"F12.wireOp",EDGE,"E403"),sQuery(id+"F12.wireOp",EDGE,"E404"),sQuery(id+"F12.wireOp",EDGE,"E405"),sQuery(id+"F12.wireOp",EDGE,"E406"),sQuery(id+"F12.wireOp",EDGE,"E407"),sQuery(id+"F12.wireOp",EDGE,"E408"),sQuery(id+"F12.wireOp",EDGE,"E409"),sQuery(id+"F12.wireOp",EDGE,"E410"),sQuery(id+"F12.wireOp",EDGE,"E411"),sQuery(id+"F12.wireOp",EDGE,"E412"),sQuery(id+"F12.wireOp",EDGE,"E413"),sQuery(id+"F12.wireOp",EDGE,"E414"),sQuery(id+"F12.wireOp",EDGE,"E415"),sQuery(id+"F12.wireOp",EDGE,"E416"),sQuery(id+"F12.wireOp",EDGE,"E417"),sQuery(id+"F12.wireOp",EDGE,"E418"),sQuery(id+"F12.wireOp",EDGE,"E419"),sQuery(id+"F12.wireOp",EDGE,"E420"),sQuery(id+"F12.wireOp",EDGE,"E421"),sQuery(id+"F12.wireOp",EDGE,"E422"),sQuery(id+"F12.wireOp",EDGE,"E423"),sQuery(id+"F12.wireOp",EDGE,"E424"),sQuery(id+"F12.wireOp",EDGE,"E425"),sQuery(id+"F12.wireOp",EDGE,"E426"),sQuery(id+"F12.wireOp",EDGE,"E427"),sQuery(id+"F12.wireOp",EDGE,"E428"),sQuery(id+"F12.wireOp",EDGE,"E429"),sQuery(id+"F12.wireOp",EDGE,"E430"),sQuery(id+"F12.wireOp",EDGE,"E431"),sQuery(id+"F12.wireOp",EDGE,"E432"),sQuery(id+"F12.wireOp",EDGE,"E433"),sQuery(id+"F12.wireOp",EDGE,"E434"),sQuery(id+"F12.wireOp",EDGE,"E435"),sQuery(id+"F12.wireOp",EDGE,"E436"),sQuery(id+"F12.wireOp",EDGE,"E437"),sQuery(id+"F12.wireOp",EDGE,"E438"),sQuery(id+"F12.wireOp",EDGE,"E439"),sQuery(id+"F12.wireOp",EDGE,"E440"),sQuery(id+"F12.wireOp",EDGE,"E441"),sQuery(id+"F12.wireOp",EDGE,"E442"),sQuery(id+"F12.wireOp",EDGE,"E443"),sQuery(id+"F12.wireOp",EDGE,"E444"),sQuery(id+"F12.wireOp",EDGE,"E445"),sQuery(id+"F12.wireOp",EDGE,"E446"),sQuery(id+"F12.wireOp",EDGE,"E447"),sQuery(id+"F12.wireOp",EDGE,"E448"),sQuery(id+"F12.wireOp",EDGE,"E449"),sQuery(id+"F12.wireOp",EDGE,"E450"),sQuery(id+"F12.wireOp",EDGE,"E451"),sQuery(id+"F12.wireOp",EDGE,"E452"),sQuery(id+"F12.wireOp",EDGE,"E453"),sQuery(id+"F12.wireOp",EDGE,"E454"),sQuery(id+"F12.wireOp",EDGE,"E455"),sQuery(id+"F12.wireOp",EDGE,"E456"),sQuery(id+"F12.wireOp",EDGE,"E457"),sQuery(id+"F12.wireOp",EDGE,"E458"),sQuery(id+"F12.wireOp",EDGE,"E459"),sQuery(id+"F12.wireOp",EDGE,"E460"),sQuery(id+"F12.wireOp",EDGE,"E461"),sQuery(id+"F12.wireOp",EDGE,"E462"),sQuery(id+"F12.wireOp",EDGE,"E463"),sQuery(id+"F12.wireOp",EDGE,"E464"),sQuery(id+"F12.wireOp",EDGE,"E465"),sQuery(id+"F12.wireOp",EDGE,"E466"),sQuery(id+"F12.wireOp",EDGE,"E467"),sQuery(id+"F12.wireOp",EDGE,"E468"),sQuery(id+"F12.wireOp",EDGE,"E469"),sQuery(id+"F12.wireOp",EDGE,"E470"),sQuery(id+"F12.wireOp",EDGE,"E471"),sQuery(id+"F12.wireOp",EDGE,"E472"),sQuery(id+"F12.wireOp",EDGE,"E473"),sQuery(id+"F12.wireOp",EDGE,"E474"),sQuery(id+"F12.wireOp",EDGE,"E475"),sQuery(id+"F12.wireOp",EDGE,"E476"),sQuery(id+"F12.wireOp",EDGE,"E477"),sQuery(id+"F12.wireOp",EDGE,"E478"),sQuery(id+"F12.wireOp",EDGE,"E480"),sQuery(id+"F12.wireOp",EDGE,"E481"),sQuery(id+"F12.wireOp",EDGE,"E482"),sQuery(id+"F12.wireOp",EDGE,"E483"),sQuery(id+"F12.wireOp",EDGE,"E484"),sQuery(id+"F12.wireOp",EDGE,"E485"),sQuery(id+"F12.wireOp",EDGE,"E486"),sQuery(id+"F12.wireOp",EDGE,"E487"),sQuery(id+"F12.wireOp",EDGE,"E488"),sQuery(id+"F12.wireOp",EDGE,"E489"),sQuery(id+"F12.wireOp",EDGE,"E490"),sQuery(id+"F12.wireOp",EDGE,"E491"),sQuery(id+"F12.wireOp",EDGE,"E492"),sQuery(id+"F12.wireOp",EDGE,"E493"),sQuery(id+"F12.wireOp",EDGE,"E494"),sQuery(id+"F12.wireOp",EDGE,"E495"),sQuery(id+"F12.wireOp",EDGE,"E496"),sQuery(id+"F12.wireOp",EDGE,"E497"),sQuery(id+"F12.wireOp",EDGE,"E498"),sQuery(id+"F12.wireOp",EDGE,"E499"),sQuery(id+"F12.wireOp",EDGE,"E500"),sQuery(id+"F12.wireOp",EDGE,"E501"),sQuery(id+"F12.wireOp",EDGE,"E502"),sQuery(id+"F12.wireOp",EDGE,"E503"),sQuery(id+"F12.wireOp",EDGE,"E504"),sQuery(id+"F12.wireOp",EDGE,"E505"),sQuery(id+"F12.wireOp",EDGE,"E506"),sQuery(id+"F12.wireOp",EDGE,"E507"),sQuery(id+"F12.wireOp",EDGE,"E508"),sQuery(id+"F12.wireOp",EDGE,"E509"),sQuery(id+"F12.wireOp",EDGE,"E510"),sQuery(id+"F12.wireOp",EDGE,"E511"),sQuery(id+"F12.wireOp",EDGE,"E512"),sQuery(id+"F12.wireOp",EDGE,"E513"),sQuery(id+"F12.wireOp",EDGE,"E514"),sQuery(id+"F12.wireOp",EDGE,"E515"),sQuery(id+"F12.wireOp",EDGE,"E516"),sQuery(id+"F12.wireOp",EDGE,"E517"),sQuery(id+"F12.wireOp",EDGE,"E518"),sQuery(id+"F12.wireOp",EDGE,"E519"),sQuery(id+"F12.wireOp",EDGE,"E520"),sQuery(id+"F12.wireOp",EDGE,"E521"),sQuery(id+"F12.wireOp",EDGE,"E522"),sQuery(id+"F12.wireOp",EDGE,"E523")])]});
            transform(context, id + "F14", {"entities" : qUnion([Q0]), "transformType" : TransformType.TRANSLATION_3D, "dx" : 0 * mm, "dy" : 0 * mm, "dz" : 470 * mm, "makeCopy" : true});
        }
        {
            var Q0;
            Q0=makeQuery(id+"F13.opExtrude","SWEPT_BODY",BODY,{"disambiguationData":[OSD([sQuery(id+"F12.wireOp",EDGE,"E402"),sQuery(id+"F12.wireOp",EDGE,"E403"),sQuery(id+"F12.wireOp",EDGE,"E404"),sQuery(id+"F12.wireOp",EDGE,"E405"),sQuery(id+"F12.wireOp",EDGE,"E406"),sQuery(id+"F12.wireOp",EDGE,"E407"),sQuery(id+"F12.wireOp",EDGE,"E408"),sQuery(id+"F12.wireOp",EDGE,"E409"),sQuery(id+"F12.wireOp",EDGE,"E410"),sQuery(id+"F12.wireOp",EDGE,"E411"),sQuery(id+"F12.wireOp",EDGE,"E412"),sQuery(id+"F12.wireOp",EDGE,"E413"),sQuery(id+"F12.wireOp",EDGE,"E414"),sQuery(id+"F12.wireOp",EDGE,"E415"),sQuery(id+"F12.wireOp",EDGE,"E416"),sQuery(id+"F12.wireOp",EDGE,"E417"),sQuery(id+"F12.wireOp",EDGE,"E418"),sQuery(id+"F12.wireOp",EDGE,"E419"),sQuery(id+"F12.wireOp",EDGE,"E420"),sQuery(id+"F12.wireOp",EDGE,"E421"),sQuery(id+"F12.wireOp",EDGE,"E422"),sQuery(id+"F12.wireOp",EDGE,"E423"),sQuery(id+"F12.wireOp",EDGE,"E424"),sQuery(id+"F12.wireOp",EDGE,"E425"),sQuery(id+"F12.wireOp",EDGE,"E426"),sQuery(id+"F12.wireOp",EDGE,"E427"),sQuery(id+"F12.wireOp",EDGE,"E428"),sQuery(id+"F12.wireOp",EDGE,"E429"),sQuery(id+"F12.wireOp",EDGE,"E430"),sQuery(id+"F12.wireOp",EDGE,"E431"),sQuery(id+"F12.wireOp",EDGE,"E432"),sQuery(id+"F12.wireOp",EDGE,"E433"),sQuery(id+"F12.wireOp",EDGE,"E434"),sQuery(id+"F12.wireOp",EDGE,"E435"),sQuery(id+"F12.wireOp",EDGE,"E436"),sQuery(id+"F12.wireOp",EDGE,"E437"),sQuery(id+"F12.wireOp",EDGE,"E438"),sQuery(id+"F12.wireOp",EDGE,"E439"),sQuery(id+"F12.wireOp",EDGE,"E440"),sQuery(id+"F12.wireOp",EDGE,"E441"),sQuery(id+"F12.wireOp",EDGE,"E442"),sQuery(id+"F12.wireOp",EDGE,"E443"),sQuery(id+"F12.wireOp",EDGE,"E444"),sQuery(id+"F12.wireOp",EDGE,"E445"),sQuery(id+"F12.wireOp",EDGE,"E446"),sQuery(id+"F12.wireOp",EDGE,"E447"),sQuery(id+"F12.wireOp",EDGE,"E448"),sQuery(id+"F12.wireOp",EDGE,"E449"),sQuery(id+"F12.wireOp",EDGE,"E450"),sQuery(id+"F12.wireOp",EDGE,"E451"),sQuery(id+"F12.wireOp",EDGE,"E452"),sQuery(id+"F12.wireOp",EDGE,"E453"),sQuery(id+"F12.wireOp",EDGE,"E454"),sQuery(id+"F12.wireOp",EDGE,"E455"),sQuery(id+"F12.wireOp",EDGE,"E456"),sQuery(id+"F12.wireOp",EDGE,"E457"),sQuery(id+"F12.wireOp",EDGE,"E458"),sQuery(id+"F12.wireOp",EDGE,"E459"),sQuery(id+"F12.wireOp",EDGE,"E460"),sQuery(id+"F12.wireOp",EDGE,"E461"),sQuery(id+"F12.wireOp",EDGE,"E462"),sQuery(id+"F12.wireOp",EDGE,"E463"),sQuery(id+"F12.wireOp",EDGE,"E464"),sQuery(id+"F12.wireOp",EDGE,"E465"),sQuery(id+"F12.wireOp",EDGE,"E466"),sQuery(id+"F12.wireOp",EDGE,"E467"),sQuery(id+"F12.wireOp",EDGE,"E468"),sQuery(id+"F12.wireOp",EDGE,"E469"),sQuery(id+"F12.wireOp",EDGE,"E470"),sQuery(id+"F12.wireOp",EDGE,"E471"),sQuery(id+"F12.wireOp",EDGE,"E472"),sQuery(id+"F12.wireOp",EDGE,"E473"),sQuery(id+"F12.wireOp",EDGE,"E474"),sQuery(id+"F12.wireOp",EDGE,"E475"),sQuery(id+"F12.wireOp",EDGE,"E476"),sQuery(id+"F12.wireOp",EDGE,"E477"),sQuery(id+"F12.wireOp",EDGE,"E478"),sQuery(id+"F12.wireOp",EDGE,"E480"),sQuery(id+"F12.wireOp",EDGE,"E481"),sQuery(id+"F12.wireOp",EDGE,"E482"),sQuery(id+"F12.wireOp",EDGE,"E483"),sQuery(id+"F12.wireOp",EDGE,"E484"),sQuery(id+"F12.wireOp",EDGE,"E485"),sQuery(id+"F12.wireOp",EDGE,"E486"),sQuery(id+"F12.wireOp",EDGE,"E487"),sQuery(id+"F12.wireOp",EDGE,"E488"),sQuery(id+"F12.wireOp",EDGE,"E489"),sQuery(id+"F12.wireOp",EDGE,"E490"),sQuery(id+"F12.wireOp",EDGE,"E491"),sQuery(id+"F12.wireOp",EDGE,"E492"),sQuery(id+"F12.wireOp",EDGE,"E493"),sQuery(id+"F12.wireOp",EDGE,"E494"),sQuery(id+"F12.wireOp",EDGE,"E495"),sQuery(id+"F12.wireOp",EDGE,"E496"),sQuery(id+"F12.wireOp",EDGE,"E497"),sQuery(id+"F12.wireOp",EDGE,"E498"),sQuery(id+"F12.wireOp",EDGE,"E499"),sQuery(id+"F12.wireOp",EDGE,"E500"),sQuery(id+"F12.wireOp",EDGE,"E501"),sQuery(id+"F12.wireOp",EDGE,"E502"),sQuery(id+"F12.wireOp",EDGE,"E503"),sQuery(id+"F12.wireOp",EDGE,"E504"),sQuery(id+"F12.wireOp",EDGE,"E505"),sQuery(id+"F12.wireOp",EDGE,"E506"),sQuery(id+"F12.wireOp",EDGE,"E507"),sQuery(id+"F12.wireOp",EDGE,"E508"),sQuery(id+"F12.wireOp",EDGE,"E509"),sQuery(id+"F12.wireOp",EDGE,"E510"),sQuery(id+"F12.wireOp",EDGE,"E511"),sQuery(id+"F12.wireOp",EDGE,"E512"),sQuery(id+"F12.wireOp",EDGE,"E513"),sQuery(id+"F12.wireOp",EDGE,"E514"),sQuery(id+"F12.wireOp",EDGE,"E515"),sQuery(id+"F12.wireOp",EDGE,"E516"),sQuery(id+"F12.wireOp",EDGE,"E517"),sQuery(id+"F12.wireOp",EDGE,"E518"),sQuery(id+"F12.wireOp",EDGE,"E519"),sQuery(id+"F12.wireOp",EDGE,"E520"),sQuery(id+"F12.wireOp",EDGE,"E521"),sQuery(id+"F12.wireOp",EDGE,"E522"),sQuery(id+"F12.wireOp",EDGE,"E523")])]});
            var Q1;
            Q1=makeQuery(id+"F14.opPattern","COPY",BODY,{"derivedFrom":makeQuery(id+"F13.opExtrude","SWEPT_BODY",BODY,{"disambiguationData":[OSD([sQuery(id+"F12.wireOp",EDGE,"E402"),sQuery(id+"F12.wireOp",EDGE,"E403"),sQuery(id+"F12.wireOp",EDGE,"E404"),sQuery(id+"F12.wireOp",EDGE,"E405"),sQuery(id+"F12.wireOp",EDGE,"E406"),sQuery(id+"F12.wireOp",EDGE,"E407"),sQuery(id+"F12.wireOp",EDGE,"E408"),sQuery(id+"F12.wireOp",EDGE,"E409"),sQuery(id+"F12.wireOp",EDGE,"E410"),sQuery(id+"F12.wireOp",EDGE,"E411"),sQuery(id+"F12.wireOp",EDGE,"E412"),sQuery(id+"F12.wireOp",EDGE,"E413"),sQuery(id+"F12.wireOp",EDGE,"E414"),sQuery(id+"F12.wireOp",EDGE,"E415"),sQuery(id+"F12.wireOp",EDGE,"E416"),sQuery(id+"F12.wireOp",EDGE,"E417"),sQuery(id+"F12.wireOp",EDGE,"E418"),sQuery(id+"F12.wireOp",EDGE,"E419"),sQuery(id+"F12.wireOp",EDGE,"E420"),sQuery(id+"F12.wireOp",EDGE,"E421"),sQuery(id+"F12.wireOp",EDGE,"E422"),sQuery(id+"F12.wireOp",EDGE,"E423"),sQuery(id+"F12.wireOp",EDGE,"E424"),sQuery(id+"F12.wireOp",EDGE,"E425"),sQuery(id+"F12.wireOp",EDGE,"E426"),sQuery(id+"F12.wireOp",EDGE,"E427"),sQuery(id+"F12.wireOp",EDGE,"E428"),sQuery(id+"F12.wireOp",EDGE,"E429"),sQuery(id+"F12.wireOp",EDGE,"E430"),sQuery(id+"F12.wireOp",EDGE,"E431"),sQuery(id+"F12.wireOp",EDGE,"E432"),sQuery(id+"F12.wireOp",EDGE,"E433"),sQuery(id+"F12.wireOp",EDGE,"E434"),sQuery(id+"F12.wireOp",EDGE,"E435"),sQuery(id+"F12.wireOp",EDGE,"E436"),sQuery(id+"F12.wireOp",EDGE,"E437"),sQuery(id+"F12.wireOp",EDGE,"E438"),sQuery(id+"F12.wireOp",EDGE,"E439"),sQuery(id+"F12.wireOp",EDGE,"E440"),sQuery(id+"F12.wireOp",EDGE,"E441"),sQuery(id+"F12.wireOp",EDGE,"E442"),sQuery(id+"F12.wireOp",EDGE,"E443"),sQuery(id+"F12.wireOp",EDGE,"E444"),sQuery(id+"F12.wireOp",EDGE,"E445"),sQuery(id+"F12.wireOp",EDGE,"E446"),sQuery(id+"F12.wireOp",EDGE,"E447"),sQuery(id+"F12.wireOp",EDGE,"E448"),sQuery(id+"F12.wireOp",EDGE,"E449"),sQuery(id+"F12.wireOp",EDGE,"E450"),sQuery(id+"F12.wireOp",EDGE,"E451"),sQuery(id+"F12.wireOp",EDGE,"E452"),sQuery(id+"F12.wireOp",EDGE,"E453"),sQuery(id+"F12.wireOp",EDGE,"E454"),sQuery(id+"F12.wireOp",EDGE,"E455"),sQuery(id+"F12.wireOp",EDGE,"E456"),sQuery(id+"F12.wireOp",EDGE,"E457"),sQuery(id+"F12.wireOp",EDGE,"E458"),sQuery(id+"F12.wireOp",EDGE,"E459"),sQuery(id+"F12.wireOp",EDGE,"E460"),sQuery(id+"F12.wireOp",EDGE,"E461"),sQuery(id+"F12.wireOp",EDGE,"E462"),sQuery(id+"F12.wireOp",EDGE,"E463"),sQuery(id+"F12.wireOp",EDGE,"E464"),sQuery(id+"F12.wireOp",EDGE,"E465"),sQuery(id+"F12.wireOp",EDGE,"E466"),sQuery(id+"F12.wireOp",EDGE,"E467"),sQuery(id+"F12.wireOp",EDGE,"E468"),sQuery(id+"F12.wireOp",EDGE,"E469"),sQuery(id+"F12.wireOp",EDGE,"E470"),sQuery(id+"F12.wireOp",EDGE,"E471"),sQuery(id+"F12.wireOp",EDGE,"E472"),sQuery(id+"F12.wireOp",EDGE,"E473"),sQuery(id+"F12.wireOp",EDGE,"E474"),sQuery(id+"F12.wireOp",EDGE,"E475"),sQuery(id+"F12.wireOp",EDGE,"E476"),sQuery(id+"F12.wireOp",EDGE,"E477"),sQuery(id+"F12.wireOp",EDGE,"E478"),sQuery(id+"F12.wireOp",EDGE,"E480"),sQuery(id+"F12.wireOp",EDGE,"E481"),sQuery(id+"F12.wireOp",EDGE,"E482"),sQuery(id+"F12.wireOp",EDGE,"E483"),sQuery(id+"F12.wireOp",EDGE,"E484"),sQuery(id+"F12.wireOp",EDGE,"E485"),sQuery(id+"F12.wireOp",EDGE,"E486"),sQuery(id+"F12.wireOp",EDGE,"E487"),sQuery(id+"F12.wireOp",EDGE,"E488"),sQuery(id+"F12.wireOp",EDGE,"E489"),sQuery(id+"F12.wireOp",EDGE,"E490"),sQuery(id+"F12.wireOp",EDGE,"E491"),sQuery(id+"F12.wireOp",EDGE,"E492"),sQuery(id+"F12.wireOp",EDGE,"E493"),sQuery(id+"F12.wireOp",EDGE,"E494"),sQuery(id+"F12.wireOp",EDGE,"E495"),sQuery(id+"F12.wireOp",EDGE,"E496"),sQuery(id+"F12.wireOp",EDGE,"E497"),sQuery(id+"F12.wireOp",EDGE,"E498"),sQuery(id+"F12.wireOp",EDGE,"E499"),sQuery(id+"F12.wireOp",EDGE,"E500"),sQuery(id+"F12.wireOp",EDGE,"E501"),sQuery(id+"F12.wireOp",EDGE,"E502"),sQuery(id+"F12.wireOp",EDGE,"E503"),sQuery(id+"F12.wireOp",EDGE,"E504"),sQuery(id+"F12.wireOp",EDGE,"E505"),sQuery(id+"F12.wireOp",EDGE,"E506"),sQuery(id+"F12.wireOp",EDGE,"E507"),sQuery(id+"F12.wireOp",EDGE,"E508"),sQuery(id+"F12.wireOp",EDGE,"E509"),sQuery(id+"F12.wireOp",EDGE,"E510"),sQuery(id+"F12.wireOp",EDGE,"E511"),sQuery(id+"F12.wireOp",EDGE,"E512"),sQuery(id+"F12.wireOp",EDGE,"E513"),sQuery(id+"F12.wireOp",EDGE,"E514"),sQuery(id+"F12.wireOp",EDGE,"E515"),sQuery(id+"F12.wireOp",EDGE,"E516"),sQuery(id+"F12.wireOp",EDGE,"E517"),sQuery(id+"F12.wireOp",EDGE,"E518"),sQuery(id+"F12.wireOp",EDGE,"E519"),sQuery(id+"F12.wireOp",EDGE,"E520"),sQuery(id+"F12.wireOp",EDGE,"E521"),sQuery(id+"F12.wireOp",EDGE,"E522"),sQuery(id+"F12.wireOp",EDGE,"E523")])]}),"instanceName":"1"});
            transform(context, id + "F15", {"entities" : qUnion([Q0, Q1]), "transformType" : TransformType.TRANSLATION_3D, "dx" : -740 * mm, "dy" : 0 * mm, "dz" : 0 * mm, "makeCopy" : true});
        }
        {
            var Q0;
            Q0=makeQuery(id+"F13.opExtrude","SWEPT_BODY",BODY,{"disambiguationData":[OSD([sQuery(id+"F12.wireOp",EDGE,"E402"),sQuery(id+"F12.wireOp",EDGE,"E403"),sQuery(id+"F12.wireOp",EDGE,"E404"),sQuery(id+"F12.wireOp",EDGE,"E405"),sQuery(id+"F12.wireOp",EDGE,"E406"),sQuery(id+"F12.wireOp",EDGE,"E407"),sQuery(id+"F12.wireOp",EDGE,"E408"),sQuery(id+"F12.wireOp",EDGE,"E409"),sQuery(id+"F12.wireOp",EDGE,"E410"),sQuery(id+"F12.wireOp",EDGE,"E411"),sQuery(id+"F12.wireOp",EDGE,"E412"),sQuery(id+"F12.wireOp",EDGE,"E413"),sQuery(id+"F12.wireOp",EDGE,"E414"),sQuery(id+"F12.wireOp",EDGE,"E415"),sQuery(id+"F12.wireOp",EDGE,"E416"),sQuery(id+"F12.wireOp",EDGE,"E417"),sQuery(id+"F12.wireOp",EDGE,"E418"),sQuery(id+"F12.wireOp",EDGE,"E419"),sQuery(id+"F12.wireOp",EDGE,"E420"),sQuery(id+"F12.wireOp",EDGE,"E421"),sQuery(id+"F12.wireOp",EDGE,"E422"),sQuery(id+"F12.wireOp",EDGE,"E423"),sQuery(id+"F12.wireOp",EDGE,"E424"),sQuery(id+"F12.wireOp",EDGE,"E425"),sQuery(id+"F12.wireOp",EDGE,"E426"),sQuery(id+"F12.wireOp",EDGE,"E427"),sQuery(id+"F12.wireOp",EDGE,"E428"),sQuery(id+"F12.wireOp",EDGE,"E429"),sQuery(id+"F12.wireOp",EDGE,"E430"),sQuery(id+"F12.wireOp",EDGE,"E431"),sQuery(id+"F12.wireOp",EDGE,"E432"),sQuery(id+"F12.wireOp",EDGE,"E433"),sQuery(id+"F12.wireOp",EDGE,"E434"),sQuery(id+"F12.wireOp",EDGE,"E435"),sQuery(id+"F12.wireOp",EDGE,"E436"),sQuery(id+"F12.wireOp",EDGE,"E437"),sQuery(id+"F12.wireOp",EDGE,"E438"),sQuery(id+"F12.wireOp",EDGE,"E439"),sQuery(id+"F12.wireOp",EDGE,"E440"),sQuery(id+"F12.wireOp",EDGE,"E441"),sQuery(id+"F12.wireOp",EDGE,"E442"),sQuery(id+"F12.wireOp",EDGE,"E443"),sQuery(id+"F12.wireOp",EDGE,"E444"),sQuery(id+"F12.wireOp",EDGE,"E445"),sQuery(id+"F12.wireOp",EDGE,"E446"),sQuery(id+"F12.wireOp",EDGE,"E447"),sQuery(id+"F12.wireOp",EDGE,"E448"),sQuery(id+"F12.wireOp",EDGE,"E449"),sQuery(id+"F12.wireOp",EDGE,"E450"),sQuery(id+"F12.wireOp",EDGE,"E451"),sQuery(id+"F12.wireOp",EDGE,"E452"),sQuery(id+"F12.wireOp",EDGE,"E453"),sQuery(id+"F12.wireOp",EDGE,"E454"),sQuery(id+"F12.wireOp",EDGE,"E455"),sQuery(id+"F12.wireOp",EDGE,"E456"),sQuery(id+"F12.wireOp",EDGE,"E457"),sQuery(id+"F12.wireOp",EDGE,"E458"),sQuery(id+"F12.wireOp",EDGE,"E459"),sQuery(id+"F12.wireOp",EDGE,"E460"),sQuery(id+"F12.wireOp",EDGE,"E461"),sQuery(id+"F12.wireOp",EDGE,"E462"),sQuery(id+"F12.wireOp",EDGE,"E463"),sQuery(id+"F12.wireOp",EDGE,"E464"),sQuery(id+"F12.wireOp",EDGE,"E465"),sQuery(id+"F12.wireOp",EDGE,"E466"),sQuery(id+"F12.wireOp",EDGE,"E467"),sQuery(id+"F12.wireOp",EDGE,"E468"),sQuery(id+"F12.wireOp",EDGE,"E469"),sQuery(id+"F12.wireOp",EDGE,"E470"),sQuery(id+"F12.wireOp",EDGE,"E471"),sQuery(id+"F12.wireOp",EDGE,"E472"),sQuery(id+"F12.wireOp",EDGE,"E473"),sQuery(id+"F12.wireOp",EDGE,"E474"),sQuery(id+"F12.wireOp",EDGE,"E475"),sQuery(id+"F12.wireOp",EDGE,"E476"),sQuery(id+"F12.wireOp",EDGE,"E477"),sQuery(id+"F12.wireOp",EDGE,"E478"),sQuery(id+"F12.wireOp",EDGE,"E480"),sQuery(id+"F12.wireOp",EDGE,"E481"),sQuery(id+"F12.wireOp",EDGE,"E482"),sQuery(id+"F12.wireOp",EDGE,"E483"),sQuery(id+"F12.wireOp",EDGE,"E484"),sQuery(id+"F12.wireOp",EDGE,"E485"),sQuery(id+"F12.wireOp",EDGE,"E486"),sQuery(id+"F12.wireOp",EDGE,"E487"),sQuery(id+"F12.wireOp",EDGE,"E488"),sQuery(id+"F12.wireOp",EDGE,"E489"),sQuery(id+"F12.wireOp",EDGE,"E490"),sQuery(id+"F12.wireOp",EDGE,"E491"),sQuery(id+"F12.wireOp",EDGE,"E492"),sQuery(id+"F12.wireOp",EDGE,"E493"),sQuery(id+"F12.wireOp",EDGE,"E494"),sQuery(id+"F12.wireOp",EDGE,"E495"),sQuery(id+"F12.wireOp",EDGE,"E496"),sQuery(id+"F12.wireOp",EDGE,"E497"),sQuery(id+"F12.wireOp",EDGE,"E498"),sQuery(id+"F12.wireOp",EDGE,"E499"),sQuery(id+"F12.wireOp",EDGE,"E500"),sQuery(id+"F12.wireOp",EDGE,"E501"),sQuery(id+"F12.wireOp",EDGE,"E502"),sQuery(id+"F12.wireOp",EDGE,"E503"),sQuery(id+"F12.wireOp",EDGE,"E504"),sQuery(id+"F12.wireOp",EDGE,"E505"),sQuery(id+"F12.wireOp",EDGE,"E506"),sQuery(id+"F12.wireOp",EDGE,"E507"),sQuery(id+"F12.wireOp",EDGE,"E508"),sQuery(id+"F12.wireOp",EDGE,"E509"),sQuery(id+"F12.wireOp",EDGE,"E510"),sQuery(id+"F12.wireOp",EDGE,"E511"),sQuery(id+"F12.wireOp",EDGE,"E512"),sQuery(id+"F12.wireOp",EDGE,"E513"),sQuery(id+"F12.wireOp",EDGE,"E514"),sQuery(id+"F12.wireOp",EDGE,"E515"),sQuery(id+"F12.wireOp",EDGE,"E516"),sQuery(id+"F12.wireOp",EDGE,"E517"),sQuery(id+"F12.wireOp",EDGE,"E518"),sQuery(id+"F12.wireOp",EDGE,"E519"),sQuery(id+"F12.wireOp",EDGE,"E520"),sQuery(id+"F12.wireOp",EDGE,"E521"),sQuery(id+"F12.wireOp",EDGE,"E522"),sQuery(id+"F12.wireOp",EDGE,"E523")])]});
            var Q1;
            Q1=makeQuery(id+"F14.opPattern","COPY",BODY,{"derivedFrom":makeQuery(id+"F13.opExtrude","SWEPT_BODY",BODY,{"disambiguationData":[OSD([sQuery(id+"F12.wireOp",EDGE,"E402"),sQuery(id+"F12.wireOp",EDGE,"E403"),sQuery(id+"F12.wireOp",EDGE,"E404"),sQuery(id+"F12.wireOp",EDGE,"E405"),sQuery(id+"F12.wireOp",EDGE,"E406"),sQuery(id+"F12.wireOp",EDGE,"E407"),sQuery(id+"F12.wireOp",EDGE,"E408"),sQuery(id+"F12.wireOp",EDGE,"E409"),sQuery(id+"F12.wireOp",EDGE,"E410"),sQuery(id+"F12.wireOp",EDGE,"E411"),sQuery(id+"F12.wireOp",EDGE,"E412"),sQuery(id+"F12.wireOp",EDGE,"E413"),sQuery(id+"F12.wireOp",EDGE,"E414"),sQuery(id+"F12.wireOp",EDGE,"E415"),sQuery(id+"F12.wireOp",EDGE,"E416"),sQuery(id+"F12.wireOp",EDGE,"E417"),sQuery(id+"F12.wireOp",EDGE,"E418"),sQuery(id+"F12.wireOp",EDGE,"E419"),sQuery(id+"F12.wireOp",EDGE,"E420"),sQuery(id+"F12.wireOp",EDGE,"E421"),sQuery(id+"F12.wireOp",EDGE,"E422"),sQuery(id+"F12.wireOp",EDGE,"E423"),sQuery(id+"F12.wireOp",EDGE,"E424"),sQuery(id+"F12.wireOp",EDGE,"E425"),sQuery(id+"F12.wireOp",EDGE,"E426"),sQuery(id+"F12.wireOp",EDGE,"E427"),sQuery(id+"F12.wireOp",EDGE,"E428"),sQuery(id+"F12.wireOp",EDGE,"E429"),sQuery(id+"F12.wireOp",EDGE,"E430"),sQuery(id+"F12.wireOp",EDGE,"E431"),sQuery(id+"F12.wireOp",EDGE,"E432"),sQuery(id+"F12.wireOp",EDGE,"E433"),sQuery(id+"F12.wireOp",EDGE,"E434"),sQuery(id+"F12.wireOp",EDGE,"E435"),sQuery(id+"F12.wireOp",EDGE,"E436"),sQuery(id+"F12.wireOp",EDGE,"E437"),sQuery(id+"F12.wireOp",EDGE,"E438"),sQuery(id+"F12.wireOp",EDGE,"E439"),sQuery(id+"F12.wireOp",EDGE,"E440"),sQuery(id+"F12.wireOp",EDGE,"E441"),sQuery(id+"F12.wireOp",EDGE,"E442"),sQuery(id+"F12.wireOp",EDGE,"E443"),sQuery(id+"F12.wireOp",EDGE,"E444"),sQuery(id+"F12.wireOp",EDGE,"E445"),sQuery(id+"F12.wireOp",EDGE,"E446"),sQuery(id+"F12.wireOp",EDGE,"E447"),sQuery(id+"F12.wireOp",EDGE,"E448"),sQuery(id+"F12.wireOp",EDGE,"E449"),sQuery(id+"F12.wireOp",EDGE,"E450"),sQuery(id+"F12.wireOp",EDGE,"E451"),sQuery(id+"F12.wireOp",EDGE,"E452"),sQuery(id+"F12.wireOp",EDGE,"E453"),sQuery(id+"F12.wireOp",EDGE,"E454"),sQuery(id+"F12.wireOp",EDGE,"E455"),sQuery(id+"F12.wireOp",EDGE,"E456"),sQuery(id+"F12.wireOp",EDGE,"E457"),sQuery(id+"F12.wireOp",EDGE,"E458"),sQuery(id+"F12.wireOp",EDGE,"E459"),sQuery(id+"F12.wireOp",EDGE,"E460"),sQuery(id+"F12.wireOp",EDGE,"E461"),sQuery(id+"F12.wireOp",EDGE,"E462"),sQuery(id+"F12.wireOp",EDGE,"E463"),sQuery(id+"F12.wireOp",EDGE,"E464"),sQuery(id+"F12.wireOp",EDGE,"E465"),sQuery(id+"F12.wireOp",EDGE,"E466"),sQuery(id+"F12.wireOp",EDGE,"E467"),sQuery(id+"F12.wireOp",EDGE,"E468"),sQuery(id+"F12.wireOp",EDGE,"E469"),sQuery(id+"F12.wireOp",EDGE,"E470"),sQuery(id+"F12.wireOp",EDGE,"E471"),sQuery(id+"F12.wireOp",EDGE,"E472"),sQuery(id+"F12.wireOp",EDGE,"E473"),sQuery(id+"F12.wireOp",EDGE,"E474"),sQuery(id+"F12.wireOp",EDGE,"E475"),sQuery(id+"F12.wireOp",EDGE,"E476"),sQuery(id+"F12.wireOp",EDGE,"E477"),sQuery(id+"F12.wireOp",EDGE,"E478"),sQuery(id+"F12.wireOp",EDGE,"E480"),sQuery(id+"F12.wireOp",EDGE,"E481"),sQuery(id+"F12.wireOp",EDGE,"E482"),sQuery(id+"F12.wireOp",EDGE,"E483"),sQuery(id+"F12.wireOp",EDGE,"E484"),sQuery(id+"F12.wireOp",EDGE,"E485"),sQuery(id+"F12.wireOp",EDGE,"E486"),sQuery(id+"F12.wireOp",EDGE,"E487"),sQuery(id+"F12.wireOp",EDGE,"E488"),sQuery(id+"F12.wireOp",EDGE,"E489"),sQuery(id+"F12.wireOp",EDGE,"E490"),sQuery(id+"F12.wireOp",EDGE,"E491"),sQuery(id+"F12.wireOp",EDGE,"E492"),sQuery(id+"F12.wireOp",EDGE,"E493"),sQuery(id+"F12.wireOp",EDGE,"E494"),sQuery(id+"F12.wireOp",EDGE,"E495"),sQuery(id+"F12.wireOp",EDGE,"E496"),sQuery(id+"F12.wireOp",EDGE,"E497"),sQuery(id+"F12.wireOp",EDGE,"E498"),sQuery(id+"F12.wireOp",EDGE,"E499"),sQuery(id+"F12.wireOp",EDGE,"E500"),sQuery(id+"F12.wireOp",EDGE,"E501"),sQuery(id+"F12.wireOp",EDGE,"E502"),sQuery(id+"F12.wireOp",EDGE,"E503"),sQuery(id+"F12.wireOp",EDGE,"E504"),sQuery(id+"F12.wireOp",EDGE,"E505"),sQuery(id+"F12.wireOp",EDGE,"E506"),sQuery(id+"F12.wireOp",EDGE,"E507"),sQuery(id+"F12.wireOp",EDGE,"E508"),sQuery(id+"F12.wireOp",EDGE,"E509"),sQuery(id+"F12.wireOp",EDGE,"E510"),sQuery(id+"F12.wireOp",EDGE,"E511"),sQuery(id+"F12.wireOp",EDGE,"E512"),sQuery(id+"F12.wireOp",EDGE,"E513"),sQuery(id+"F12.wireOp",EDGE,"E514"),sQuery(id+"F12.wireOp",EDGE,"E515"),sQuery(id+"F12.wireOp",EDGE,"E516"),sQuery(id+"F12.wireOp",EDGE,"E517"),sQuery(id+"F12.wireOp",EDGE,"E518"),sQuery(id+"F12.wireOp",EDGE,"E519"),sQuery(id+"F12.wireOp",EDGE,"E520"),sQuery(id+"F12.wireOp",EDGE,"E521"),sQuery(id+"F12.wireOp",EDGE,"E522"),sQuery(id+"F12.wireOp",EDGE,"E523")])]}),"instanceName":"1"});
            transform(context, id + "F16", {"entities" : qUnion([Q0, Q1]), "transformType" : TransformType.TRANSLATION_3D, "dx" : -343 * mm, "dy" : 0 * mm, "dz" : 0 * mm, "makeCopy" : true});
        }
        {
            var Q0;
            Q0=qCreatedBy(makeId("Top.planeOp"),FACE);
            cPlane(context, id + "F17", {"entities" : qUnion([Q0]), "cplaneType" : CPlaneType.OFFSET, "offset" : 30 * mm, "width" : 150 * mm, "height" : 150 * mm});
        }
        {
            var Q0;
            Q0=qCreatedBy(id+"F17.planeOp",FACE);
            var sketch = newSketch(context, id + "F18", { "sketchPlane" : qUnion([Q0])});
            skLineSegment(sketch, "E524", {"start": v(-345.6, 15.3) * mm, "end": v(-310.3, 15.3) * mm});
            skLineSegment(sketch, "E525", {"start": v(-328, 32.6) * mm, "end": v(-328, -1.5) * mm});
            skLineSegment(sketch, "E526", {"start": v(-323.8, 25.3) * mm, "end": v(-310.3, 25.3) * mm});
            skLineSegment(sketch, "E527", {"start": v(-318, 32.6) * mm, "end": v(-318, 19.2) * mm});
            skLineSegment(sketch, "E528", {"start": v(-332.2, 25.3) * mm, "end": v(-345.7, 25.3) * mm});
            skLineSegment(sketch, "E529", {"start": v(-338, 32.6) * mm, "end": v(-338, 19.2) * mm});
            skLineSegment(sketch, "E530", {"start": v(-323.8, 5.3) * mm, "end": v(-310.3, 5.3) * mm});
            skLineSegment(sketch, "E531", {"start": v(-332.2, 5.3) * mm, "end": v(-345.7, 5.3) * mm});
            skLineSegment(sketch, "E532", {"start": v(-338, -2) * mm, "end": v(-338, 11.4) * mm});
            skLineSegment(sketch, "E533", {"start": v(-324.85, 30.3) * mm, "end": v(-324.85, 27.8) * mm});
            skLineSegment(sketch, "E534", {"start": v(-322.85, 27.8) * mm, "end": v(-322.85, 21.85) * mm});
            skLineSegment(sketch, "E535", {"start": v(-324.85, 27.8) * mm, "end": v(-322.85, 27.8) * mm});
            skLineSegment(sketch, "E536", {"start": v(-331.15, 30.3) * mm, "end": v(-331.15, 27.8) * mm});
            skLineSegment(sketch, "E537", {"start": v(-331.15, 27.8) * mm, "end": v(-333.15, 27.8) * mm});
            skLineSegment(sketch, "E538", {"start": v(-333.15, 27.8) * mm, "end": v(-333.15, 21.85) * mm});
            skLineSegment(sketch, "E539", {"start": v(-343, 18.45) * mm, "end": v(-340.5, 18.45) * mm});
            skLineSegment(sketch, "E540", {"start": v(-340.5, 20.45) * mm, "end": v(-334.55, 20.45) * mm});
            skLineSegment(sketch, "E541", {"start": v(-340.5, 18.45) * mm, "end": v(-340.5, 20.45) * mm});
            skLineSegment(sketch, "E542", {"start": v(-343, 12.15) * mm, "end": v(-340.5, 12.15) * mm});
            skLineSegment(sketch, "E543", {"start": v(-340.5, 12.15) * mm, "end": v(-340.5, 10.15) * mm});
            skLineSegment(sketch, "E544", {"start": v(-340.5, 10.15) * mm, "end": v(-334.55, 10.15) * mm});
            skLineSegment(sketch, "E545", {"start": v(-331.15, 0.3) * mm, "end": v(-331.15, 2.8) * mm});
            skLineSegment(sketch, "E546", {"start": v(-333.15, 2.8) * mm, "end": v(-333.15, 8.75) * mm});
            skLineSegment(sketch, "E547", {"start": v(-331.15, 2.8) * mm, "end": v(-333.15, 2.8) * mm});
            skLineSegment(sketch, "E548", {"start": v(-324.85, 0.3) * mm, "end": v(-324.85, 2.8) * mm});
            skLineSegment(sketch, "E549", {"start": v(-324.85, 2.8) * mm, "end": v(-322.85, 2.8) * mm});
            skLineSegment(sketch, "E550", {"start": v(-322.85, 2.8) * mm, "end": v(-322.85, 8.75) * mm});
            skLineSegment(sketch, "E551", {"start": v(-313, 12.15) * mm, "end": v(-315.5, 12.15) * mm});
            skLineSegment(sketch, "E552", {"start": v(-315.5, 10.15) * mm, "end": v(-321.45, 10.15) * mm});
            skLineSegment(sketch, "E553", {"start": v(-315.5, 12.15) * mm, "end": v(-315.5, 10.15) * mm});
            skLineSegment(sketch, "E554", {"start": v(-313, 18.45) * mm, "end": v(-315.5, 18.45) * mm});
            skLineSegment(sketch, "E555", {"start": v(-315.5, 18.45) * mm, "end": v(-315.5, 20.45) * mm});
            skLineSegment(sketch, "E556", {"start": v(-315.5, 20.45) * mm, "end": v(-321.45, 20.45) * mm});
            skLineSegment(sketch, "E557", {"start": v(-331.15, 19.8) * mm, "end": v(-331.15, 21.85) * mm});
            skLineSegment(sketch, "E558", {"start": v(-333.15, 21.85) * mm, "end": v(-331.15, 21.85) * mm});
            skLineSegment(sketch, "E559", {"start": v(-331.15, 19.8) * mm, "end": v(-322.85, 21.85) * mm});
            skLineSegment(sketch, "E560", {"start": v(-332.5, 12.15) * mm, "end": v(-334.55, 12.15) * mm});
            skLineSegment(sketch, "E561", {"start": v(-334.55, 10.15) * mm, "end": v(-334.55, 12.15) * mm});
            skLineSegment(sketch, "E562", {"start": v(-332.5, 12.15) * mm, "end": v(-334.55, 20.45) * mm});
            skLineSegment(sketch, "E563", {"start": v(-324.85, 10.8) * mm, "end": v(-324.85, 8.75) * mm});
            skLineSegment(sketch, "E564", {"start": v(-322.85, 8.75) * mm, "end": v(-324.85, 8.75) * mm});
            skLineSegment(sketch, "E565", {"start": v(-324.85, 10.8) * mm, "end": v(-333.15, 8.75) * mm});
            skLineSegment(sketch, "E566", {"start": v(-323.5, 18.45) * mm, "end": v(-321.45, 18.45) * mm});
            skLineSegment(sketch, "E567", {"start": v(-321.45, 20.45) * mm, "end": v(-321.45, 18.45) * mm});
            skLineSegment(sketch, "E568", {"start": v(-323.5, 18.45) * mm, "end": v(-321.45, 10.15) * mm});
            skCircle(sketch, "E569", {"center": v(-328, 15.3) * mm, "radius": 2.5 * mm});
            skLineSegment(sketch, "E570", {"start": v(-315, 26.54) * mm, "end": v(-316.76, 28.3) * mm});
            skLineSegment(sketch, "E571", {"start": v(-316.76, 28.3) * mm, "end": v(-319.24, 28.3) * mm});
            skLineSegment(sketch, "E572", {"start": v(-319.24, 28.3) * mm, "end": v(-321, 26.54) * mm});
            skLineSegment(sketch, "E573", {"start": v(-321, 26.54) * mm, "end": v(-321, 24.06) * mm});
            skLineSegment(sketch, "E574", {"start": v(-321, 24.06) * mm, "end": v(-319.24, 22.3) * mm});
            skLineSegment(sketch, "E575", {"start": v(-319.24, 22.3) * mm, "end": v(-316.76, 22.3) * mm});
            skLineSegment(sketch, "E576", {"start": v(-316.76, 22.3) * mm, "end": v(-315, 24.06) * mm});
            skLineSegment(sketch, "E577", {"start": v(-315, 24.06) * mm, "end": v(-315, 26.54) * mm});
            skLineSegment(sketch, "E578", {"start": v(-335, 26.54) * mm, "end": v(-336.76, 28.3) * mm});
            skLineSegment(sketch, "E579", {"start": v(-336.76, 28.3) * mm, "end": v(-339.24, 28.3) * mm});
            skLineSegment(sketch, "E580", {"start": v(-339.24, 28.3) * mm, "end": v(-341, 26.54) * mm});
            skLineSegment(sketch, "E581", {"start": v(-341, 26.54) * mm, "end": v(-341, 24.06) * mm});
            skLineSegment(sketch, "E582", {"start": v(-341, 24.06) * mm, "end": v(-339.24, 22.3) * mm});
            skLineSegment(sketch, "E583", {"start": v(-339.24, 22.3) * mm, "end": v(-336.76, 22.3) * mm});
            skLineSegment(sketch, "E584", {"start": v(-336.76, 22.3) * mm, "end": v(-335, 24.06) * mm});
            skLineSegment(sketch, "E585", {"start": v(-335, 24.06) * mm, "end": v(-335, 26.54) * mm});
            skLineSegment(sketch, "E586", {"start": v(-315, 6.54) * mm, "end": v(-316.76, 8.3) * mm});
            skLineSegment(sketch, "E587", {"start": v(-316.76, 8.3) * mm, "end": v(-319.24, 8.3) * mm});
            skLineSegment(sketch, "E588", {"start": v(-319.24, 8.3) * mm, "end": v(-321, 6.54) * mm});
            skLineSegment(sketch, "E589", {"start": v(-321, 6.54) * mm, "end": v(-321, 4.06) * mm});
            skLineSegment(sketch, "E590", {"start": v(-321, 4.06) * mm, "end": v(-319.24, 2.3) * mm});
            skLineSegment(sketch, "E591", {"start": v(-319.24, 2.3) * mm, "end": v(-316.76, 2.3) * mm});
            skLineSegment(sketch, "E592", {"start": v(-316.76, 2.3) * mm, "end": v(-315, 4.06) * mm});
            skLineSegment(sketch, "E593", {"start": v(-315, 4.06) * mm, "end": v(-315, 6.54) * mm});
            skLineSegment(sketch, "E594", {"start": v(-335, 6.54) * mm, "end": v(-336.76, 8.3) * mm});
            skLineSegment(sketch, "E595", {"start": v(-336.76, 8.3) * mm, "end": v(-339.24, 8.3) * mm});
            skLineSegment(sketch, "E596", {"start": v(-339.24, 8.3) * mm, "end": v(-341, 6.54) * mm});
            skLineSegment(sketch, "E597", {"start": v(-341, 6.54) * mm, "end": v(-341, 4.06) * mm});
            skLineSegment(sketch, "E598", {"start": v(-341, 4.06) * mm, "end": v(-339.24, 2.3) * mm});
            skLineSegment(sketch, "E599", {"start": v(-339.24, 2.3) * mm, "end": v(-336.76, 2.3) * mm});
            skLineSegment(sketch, "E600", {"start": v(-336.76, 2.3) * mm, "end": v(-335, 4.06) * mm});
            skLineSegment(sketch, "E601", {"start": v(-335, 4.06) * mm, "end": v(-335, 6.54) * mm});
            skLineSegment(sketch, "E602", {"start": v(-316.5, 30.3) * mm, "end": v(-316.5, 30) * mm});
            skLineSegment(sketch, "E603", {"start": v(-316.5, 30) * mm, "end": v(-318, 30) * mm});
            skLineSegment(sketch, "E604", {"start": v(-319.5, 30.3) * mm, "end": v(-319.5, 30) * mm});
            skLineSegment(sketch, "E605", {"start": v(-319.5, 30) * mm, "end": v(-318, 30) * mm});
            skLineSegment(sketch, "E606", {"start": v(-313, 23.8) * mm, "end": v(-313.3, 23.8) * mm});
            skLineSegment(sketch, "E607", {"start": v(-313.3, 23.8) * mm, "end": v(-313.3, 25.3) * mm});
            skLineSegment(sketch, "E608", {"start": v(-313, 26.8) * mm, "end": v(-313.3, 26.8) * mm});
            skLineSegment(sketch, "E609", {"start": v(-313.3, 26.8) * mm, "end": v(-313.3, 25.3) * mm});
            skLineSegment(sketch, "E610", {"start": v(-318, -2) * mm, "end": v(-318, 11.4) * mm});
            skLineSegment(sketch, "E611", {"start": v(-316.5, 0.3) * mm, "end": v(-316.5, 0.6) * mm});
            skLineSegment(sketch, "E612", {"start": v(-316.5, 0.6) * mm, "end": v(-318, 0.6) * mm});
            skLineSegment(sketch, "E613", {"start": v(-319.5, 0.3) * mm, "end": v(-319.5, 0.6) * mm});
            skLineSegment(sketch, "E614", {"start": v(-319.5, 0.6) * mm, "end": v(-318, 0.6) * mm});
            skLineSegment(sketch, "E615", {"start": v(-313, 6.8) * mm, "end": v(-313.3, 6.8) * mm});
            skLineSegment(sketch, "E616", {"start": v(-313.3, 6.8) * mm, "end": v(-313.3, 5.3) * mm});
            skLineSegment(sketch, "E617", {"start": v(-313, 3.8) * mm, "end": v(-313.3, 3.8) * mm});
            skLineSegment(sketch, "E618", {"start": v(-313.3, 3.8) * mm, "end": v(-313.3, 5.3) * mm});
            skLineSegment(sketch, "E619", {"start": v(-339.5, 30.3) * mm, "end": v(-339.5, 30) * mm});
            skLineSegment(sketch, "E620", {"start": v(-339.5, 30) * mm, "end": v(-338, 30) * mm});
            skLineSegment(sketch, "E621", {"start": v(-336.5, 30.3) * mm, "end": v(-336.5, 30) * mm});
            skLineSegment(sketch, "E622", {"start": v(-336.5, 30) * mm, "end": v(-338, 30) * mm});
            skLineSegment(sketch, "E623", {"start": v(-343, 23.8) * mm, "end": v(-342.7, 23.8) * mm});
            skLineSegment(sketch, "E624", {"start": v(-342.7, 23.8) * mm, "end": v(-342.7, 25.3) * mm});
            skLineSegment(sketch, "E625", {"start": v(-343, 26.8) * mm, "end": v(-342.7, 26.8) * mm});
            skLineSegment(sketch, "E626", {"start": v(-342.7, 26.8) * mm, "end": v(-342.7, 25.3) * mm});
            skLineSegment(sketch, "E627", {"start": v(-343, 6.8) * mm, "end": v(-342.7, 6.8) * mm});
            skLineSegment(sketch, "E628", {"start": v(-342.7, 6.8) * mm, "end": v(-342.7, 5.3) * mm});
            skLineSegment(sketch, "E629", {"start": v(-343, 3.8) * mm, "end": v(-342.7, 3.8) * mm});
            skLineSegment(sketch, "E630", {"start": v(-342.7, 3.8) * mm, "end": v(-342.7, 5.3) * mm});
            skLineSegment(sketch, "E631", {"start": v(-339.5, 0.3) * mm, "end": v(-339.5, 0.6) * mm});
            skLineSegment(sketch, "E632", {"start": v(-339.5, 0.6) * mm, "end": v(-338, 0.6) * mm});
            skLineSegment(sketch, "E633", {"start": v(-336.5, 0.3) * mm, "end": v(-336.5, 0.6) * mm});
            skLineSegment(sketch, "E634", {"start": v(-336.5, 0.6) * mm, "end": v(-338, 0.6) * mm});
            skLineSegment(sketch, "E635", {"start": v(-314, 30.3) * mm, "end": v(-316.5, 30.3) * mm});
            skLineSegment(sketch, "E636", {"start": v(-319.5, 30.3) * mm, "end": v(-324.85, 30.3) * mm});
            skLineSegment(sketch, "E637", {"start": v(-313, 18.45) * mm, "end": v(-313, 23.8) * mm});
            skLineSegment(sketch, "E638", {"start": v(-313, 29.3) * mm, "end": v(-313, 26.8) * mm});
            skLineSegment(sketch, "E639", {"start": v(-313, 1.3) * mm, "end": v(-313, 3.8) * mm});
            skLineSegment(sketch, "E640", {"start": v(-313, 6.8) * mm, "end": v(-313, 12.15) * mm});
            skLineSegment(sketch, "E641", {"start": v(-324.85, 0.3) * mm, "end": v(-319.5, 0.3) * mm});
            skLineSegment(sketch, "E642", {"start": v(-314, 0.3) * mm, "end": v(-316.5, 0.3) * mm});
            skLineSegment(sketch, "E643", {"start": v(-342, 0.3) * mm, "end": v(-339.5, 0.3) * mm});
            skLineSegment(sketch, "E644", {"start": v(-336.5, 0.3) * mm, "end": v(-331.15, 0.3) * mm});
            skLineSegment(sketch, "E645", {"start": v(-343, 12.15) * mm, "end": v(-343, 6.8) * mm});
            skLineSegment(sketch, "E646", {"start": v(-343, 1.3) * mm, "end": v(-343, 3.8) * mm});
            skLineSegment(sketch, "E647", {"start": v(-343, 29.3) * mm, "end": v(-343, 26.8) * mm});
            skLineSegment(sketch, "E648", {"start": v(-343, 23.8) * mm, "end": v(-343, 18.45) * mm});
            skLineSegment(sketch, "E649", {"start": v(-331.15, 30.3) * mm, "end": v(-336.5, 30.3) * mm});
            skLineSegment(sketch, "E650", {"start": v(-342, 30.3) * mm, "end": v(-339.5, 30.3) * mm});
            skLineSegment(sketch, "E651", {"start": v(-342, 30.3) * mm, "end": v(-343, 29.3) * mm});
            skLineSegment(sketch, "E652", {"start": v(-343, 1.3) * mm, "end": v(-342, 0.3) * mm});
            skLineSegment(sketch, "E653", {"start": v(-314, 0.3) * mm, "end": v(-313, 1.3) * mm});
            skLineSegment(sketch, "E654", {"start": v(-313, 29.3) * mm, "end": v(-314, 30.3) * mm});
            skSolve(sketch);
        }
        {
            var Q0;
            Q0 = qSketchRegion(id + "F18", true);
            extrude(context, id + "F19", {"entities" : qUnion([Q0]), "depth" : 440 * mm, "offsetDistance" : 25 * mm});
        }
        {
            var Q0;
            Q0=makeQuery(id+"F19.opExtrude","SWEPT_BODY",BODY,{"disambiguationData":[OSD([sQuery(id+"F18.wireOp",EDGE,"E533"),sQuery(id+"F18.wireOp",EDGE,"E534"),sQuery(id+"F18.wireOp",EDGE,"E535"),sQuery(id+"F18.wireOp",EDGE,"E536"),sQuery(id+"F18.wireOp",EDGE,"E537"),sQuery(id+"F18.wireOp",EDGE,"E538"),sQuery(id+"F18.wireOp",EDGE,"E539"),sQuery(id+"F18.wireOp",EDGE,"E540"),sQuery(id+"F18.wireOp",EDGE,"E541"),sQuery(id+"F18.wireOp",EDGE,"E542"),sQuery(id+"F18.wireOp",EDGE,"E543"),sQuery(id+"F18.wireOp",EDGE,"E544"),sQuery(id+"F18.wireOp",EDGE,"E545"),sQuery(id+"F18.wireOp",EDGE,"E546"),sQuery(id+"F18.wireOp",EDGE,"E547"),sQuery(id+"F18.wireOp",EDGE,"E548"),sQuery(id+"F18.wireOp",EDGE,"E549"),sQuery(id+"F18.wireOp",EDGE,"E550"),sQuery(id+"F18.wireOp",EDGE,"E551"),sQuery(id+"F18.wireOp",EDGE,"E552"),sQuery(id+"F18.wireOp",EDGE,"E553"),sQuery(id+"F18.wireOp",EDGE,"E554"),sQuery(id+"F18.wireOp",EDGE,"E555"),sQuery(id+"F18.wireOp",EDGE,"E556"),sQuery(id+"F18.wireOp",EDGE,"E557"),sQuery(id+"F18.wireOp",EDGE,"E558"),sQuery(id+"F18.wireOp",EDGE,"E559"),sQuery(id+"F18.wireOp",EDGE,"E560"),sQuery(id+"F18.wireOp",EDGE,"E561"),sQuery(id+"F18.wireOp",EDGE,"E562"),sQuery(id+"F18.wireOp",EDGE,"E563"),sQuery(id+"F18.wireOp",EDGE,"E564"),sQuery(id+"F18.wireOp",EDGE,"E565"),sQuery(id+"F18.wireOp",EDGE,"E566"),sQuery(id+"F18.wireOp",EDGE,"E567"),sQuery(id+"F18.wireOp",EDGE,"E568"),sQuery(id+"F18.wireOp",EDGE,"E569"),sQuery(id+"F18.wireOp",EDGE,"E570"),sQuery(id+"F18.wireOp",EDGE,"E571"),sQuery(id+"F18.wireOp",EDGE,"E572"),sQuery(id+"F18.wireOp",EDGE,"E573"),sQuery(id+"F18.wireOp",EDGE,"E574"),sQuery(id+"F18.wireOp",EDGE,"E575"),sQuery(id+"F18.wireOp",EDGE,"E576"),sQuery(id+"F18.wireOp",EDGE,"E577"),sQuery(id+"F18.wireOp",EDGE,"E578"),sQuery(id+"F18.wireOp",EDGE,"E579"),sQuery(id+"F18.wireOp",EDGE,"E580"),sQuery(id+"F18.wireOp",EDGE,"E581"),sQuery(id+"F18.wireOp",EDGE,"E582"),sQuery(id+"F18.wireOp",EDGE,"E583"),sQuery(id+"F18.wireOp",EDGE,"E584"),sQuery(id+"F18.wireOp",EDGE,"E585"),sQuery(id+"F18.wireOp",EDGE,"E586"),sQuery(id+"F18.wireOp",EDGE,"E587"),sQuery(id+"F18.wireOp",EDGE,"E588"),sQuery(id+"F18.wireOp",EDGE,"E589"),sQuery(id+"F18.wireOp",EDGE,"E590"),sQuery(id+"F18.wireOp",EDGE,"E591"),sQuery(id+"F18.wireOp",EDGE,"E592"),sQuery(id+"F18.wireOp",EDGE,"E593"),sQuery(id+"F18.wireOp",EDGE,"E594"),sQuery(id+"F18.wireOp",EDGE,"E595"),sQuery(id+"F18.wireOp",EDGE,"E596"),sQuery(id+"F18.wireOp",EDGE,"E597"),sQuery(id+"F18.wireOp",EDGE,"E598"),sQuery(id+"F18.wireOp",EDGE,"E599"),sQuery(id+"F18.wireOp",EDGE,"E600"),sQuery(id+"F18.wireOp",EDGE,"E601"),sQuery(id+"F18.wireOp",EDGE,"E602"),sQuery(id+"F18.wireOp",EDGE,"E603"),sQuery(id+"F18.wireOp",EDGE,"E604"),sQuery(id+"F18.wireOp",EDGE,"E605"),sQuery(id+"F18.wireOp",EDGE,"E606"),sQuery(id+"F18.wireOp",EDGE,"E607"),sQuery(id+"F18.wireOp",EDGE,"E608"),sQuery(id+"F18.wireOp",EDGE,"E609"),sQuery(id+"F18.wireOp",EDGE,"E611"),sQuery(id+"F18.wireOp",EDGE,"E612"),sQuery(id+"F18.wireOp",EDGE,"E613"),sQuery(id+"F18.wireOp",EDGE,"E614"),sQuery(id+"F18.wireOp",EDGE,"E615"),sQuery(id+"F18.wireOp",EDGE,"E616"),sQuery(id+"F18.wireOp",EDGE,"E617"),sQuery(id+"F18.wireOp",EDGE,"E618"),sQuery(id+"F18.wireOp",EDGE,"E619"),sQuery(id+"F18.wireOp",EDGE,"E620"),sQuery(id+"F18.wireOp",EDGE,"E621"),sQuery(id+"F18.wireOp",EDGE,"E622"),sQuery(id+"F18.wireOp",EDGE,"E623"),sQuery(id+"F18.wireOp",EDGE,"E624"),sQuery(id+"F18.wireOp",EDGE,"E625"),sQuery(id+"F18.wireOp",EDGE,"E626"),sQuery(id+"F18.wireOp",EDGE,"E627"),sQuery(id+"F18.wireOp",EDGE,"E628"),sQuery(id+"F18.wireOp",EDGE,"E629"),sQuery(id+"F18.wireOp",EDGE,"E630"),sQuery(id+"F18.wireOp",EDGE,"E631"),sQuery(id+"F18.wireOp",EDGE,"E632"),sQuery(id+"F18.wireOp",EDGE,"E633"),sQuery(id+"F18.wireOp",EDGE,"E634"),sQuery(id+"F18.wireOp",EDGE,"E635"),sQuery(id+"F18.wireOp",EDGE,"E636"),sQuery(id+"F18.wireOp",EDGE,"E637"),sQuery(id+"F18.wireOp",EDGE,"E638"),sQuery(id+"F18.wireOp",EDGE,"E639"),sQuery(id+"F18.wireOp",EDGE,"E640"),sQuery(id+"F18.wireOp",EDGE,"E641"),sQuery(id+"F18.wireOp",EDGE,"E642"),sQuery(id+"F18.wireOp",EDGE,"E643"),sQuery(id+"F18.wireOp",EDGE,"E644"),sQuery(id+"F18.wireOp",EDGE,"E645"),sQuery(id+"F18.wireOp",EDGE,"E646"),sQuery(id+"F18.wireOp",EDGE,"E647"),sQuery(id+"F18.wireOp",EDGE,"E648"),sQuery(id+"F18.wireOp",EDGE,"E649"),sQuery(id+"F18.wireOp",EDGE,"E650"),sQuery(id+"F18.wireOp",EDGE,"E651"),sQuery(id+"F18.wireOp",EDGE,"E652"),sQuery(id+"F18.wireOp",EDGE,"E653"),sQuery(id+"F18.wireOp",EDGE,"E654")])]});
            transform(context, id + "F20", {"entities" : qUnion([Q0]), "transformType" : TransformType.TRANSLATION_3D, "dx" : 0 * mm, "dy" : 640 * mm, "dz" : 0 * mm, "makeCopy" : true});
        }
    });
